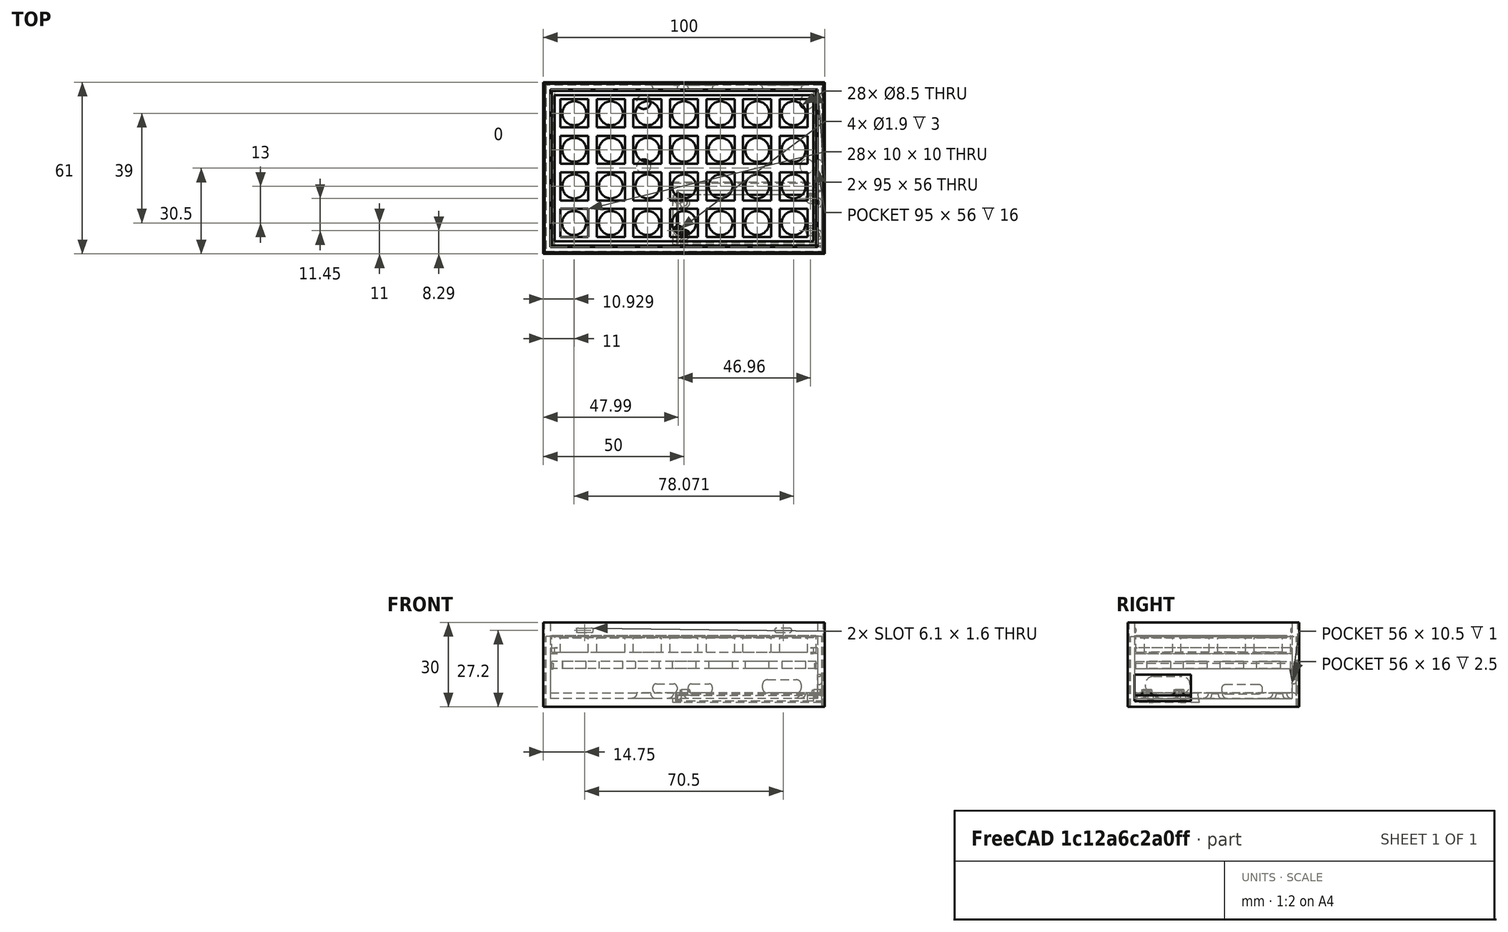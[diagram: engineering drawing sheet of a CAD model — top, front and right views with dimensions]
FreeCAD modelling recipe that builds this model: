
FCSTD DOCUMENT  (FreeCAD 1.0R39285 (Git))
Label: Contrib Cal FreeCAD
License: All rights reserved
LicenseURL: https://en.wikipedia.org/wiki/All_rights_reserved
objects: Sketcher::SketchObject×37, PartDesign::Pad×20, PartDesign::Pocket×14, PartDesign::Body×8, PartDesign::Fillet×7, Mesh::Feature×2, PartDesign::Hole×1, Measure::MeasureArea×1, Measure::MeasurePython×1
note: 208 computed .brp shape members not serialized (recipe doc carries the construction recipe); baked Part::Feature solids carry a one-line shape summary decoded from their .brp

FEATURE [Sketcher::SketchObject] Sketch
  ArcFitTolerance = 1e-06
  AttachmentSupport = -> [XY_Plane]
  FullyConstrained = true
  MakeInternals = false
  MapMode = 5
  sketch-geometry (117):
    g0: LineSegment StartX=47 StartY=-27.5 StartZ=0 EndX=47 EndY=27.5 EndZ=0
    g1: LineSegment StartX=47 StartY=27.5 StartZ=0 EndX=-47 EndY=27.5 EndZ=0
    g2: LineSegment StartX=-47 StartY=27.5 StartZ=0 EndX=-47 EndY=-27.5 EndZ=0
    g3: LineSegment StartX=-47 StartY=-27.5 StartZ=0 EndX=47 EndY=-27.5 EndZ=0
    g4: GeomPoint [constr] X=0 Y=0 Z=0
    g5: LineSegment StartX=-44 StartY=24.5 StartZ=0 EndX=-44 EndY=14.5 EndZ=0
    g6: LineSegment StartX=-44 StartY=14.5 StartZ=0 EndX=-34 EndY=14.5 EndZ=0
    g7: LineSegment StartX=-34 StartY=14.5 StartZ=0 EndX=-34 EndY=24.5 EndZ=0
    g8: LineSegment StartX=-34 StartY=24.5 StartZ=0 EndX=-44 EndY=24.5 EndZ=0
    g9: LineSegment StartX=-31 StartY=24.5 StartZ=0 EndX=-31 EndY=14.5 EndZ=0
    g10: LineSegment StartX=-31 StartY=14.5 StartZ=0 EndX=-21 EndY=14.5 EndZ=0
    g11: LineSegment StartX=-21 StartY=14.5 StartZ=0 EndX=-21 EndY=24.5 EndZ=0
    g12: LineSegment StartX=-21 StartY=24.5 StartZ=0 EndX=-31 EndY=24.5 EndZ=0
    g13: LineSegment StartX=-18 StartY=24.5 StartZ=0 EndX=-18 EndY=14.5 EndZ=0
    g14: LineSegment StartX=-18 StartY=14.5 StartZ=0 EndX=-8 EndY=14.5 EndZ=0
    g15: LineSegment StartX=-8 StartY=14.5 StartZ=0 EndX=-8 EndY=24.5 EndZ=0
    g16: LineSegment StartX=-8 StartY=24.5 StartZ=0 EndX=-18 EndY=24.5 EndZ=0
    g17: LineSegment StartX=-5 StartY=24.5 StartZ=0 EndX=-5 EndY=14.5 EndZ=0
    g18: LineSegment StartX=-5 StartY=14.5 StartZ=0 EndX=5 EndY=14.5 EndZ=0
    g19: LineSegment StartX=5 StartY=14.5 StartZ=0 EndX=5 EndY=24.5 EndZ=0
    g20: LineSegment StartX=5 StartY=24.5 StartZ=0 EndX=-5 EndY=24.5 EndZ=0
    g21: LineSegment StartX=8 StartY=24.5 StartZ=0 EndX=8 EndY=14.5 EndZ=0
    g22: LineSegment StartX=8 StartY=14.5 StartZ=0 EndX=18 EndY=14.5 EndZ=0
    g23: LineSegment StartX=18 StartY=14.5 StartZ=0 EndX=18 EndY=24.5 EndZ=0
    g24: LineSegment StartX=18 StartY=24.5 StartZ=0 EndX=8 EndY=24.5 EndZ=0
    g25: LineSegment StartX=21 StartY=24.5 StartZ=0 EndX=21 EndY=14.5 EndZ=0
    g26: LineSegment StartX=21 StartY=14.5 StartZ=0 EndX=31 EndY=14.5 EndZ=0
    g27: LineSegment StartX=31 StartY=14.5 StartZ=0 EndX=31 EndY=24.5 EndZ=0
    g28: LineSegment StartX=31 StartY=24.5 StartZ=0 EndX=21 EndY=24.5 EndZ=0
    g29: LineSegment StartX=34 StartY=24.5 StartZ=0 EndX=34 EndY=14.5 EndZ=0
    g30: LineSegment StartX=34 StartY=14.5 StartZ=0 EndX=44 EndY=14.5 EndZ=0
    g31: LineSegment StartX=44 StartY=14.5 StartZ=0 EndX=44 EndY=24.5 EndZ=0
    g32: LineSegment StartX=44 StartY=24.5 StartZ=0 EndX=34 EndY=24.5 EndZ=0
    g33: LineSegment StartX=-44 StartY=11.5 StartZ=0 EndX=-44 EndY=1.5 EndZ=0
    g34: LineSegment StartX=-44 StartY=1.5 StartZ=0 EndX=-34 EndY=1.5 EndZ=0
    g35: LineSegment StartX=-34 StartY=1.5 StartZ=0 EndX=-34 EndY=11.5 EndZ=0
    g36: LineSegment StartX=-34 StartY=11.5 StartZ=0 EndX=-44 EndY=11.5 EndZ=0
    g37: LineSegment StartX=-31 StartY=11.5 StartZ=0 EndX=-31 EndY=1.5 EndZ=0
    g38: LineSegment StartX=-31 StartY=1.5 StartZ=0 EndX=-21 EndY=1.5 EndZ=0
    g39: LineSegment StartX=-21 StartY=1.5 StartZ=0 EndX=-21 EndY=11.5 EndZ=0
    g40: LineSegment StartX=-21 StartY=11.5 StartZ=0 EndX=-31 EndY=11.5 EndZ=0
    g41: LineSegment StartX=-18 StartY=11.5 StartZ=0 EndX=-18 EndY=1.5 EndZ=0
    g42: LineSegment StartX=-18 StartY=1.5 StartZ=0 EndX=-8 EndY=1.5 EndZ=0
    g43: LineSegment StartX=-8 StartY=1.5 StartZ=0 EndX=-8 EndY=11.5 EndZ=0
    g44: LineSegment StartX=-8 StartY=11.5 StartZ=0 EndX=-18 EndY=11.5 EndZ=0
    g45: LineSegment StartX=-5 StartY=11.5 StartZ=0 EndX=-5 EndY=1.5 EndZ=0
    g46: LineSegment StartX=-5 StartY=1.5 StartZ=0 EndX=5 EndY=1.5 EndZ=0
    g47: LineSegment StartX=5 StartY=1.5 StartZ=0 EndX=5 EndY=11.5 EndZ=0
    g48: LineSegment StartX=5 StartY=11.5 StartZ=0 EndX=-5 EndY=11.5 EndZ=0
    g49: LineSegment StartX=8 StartY=11.5 StartZ=0 EndX=8 EndY=1.5 EndZ=0
    g50: LineSegment StartX=8 StartY=1.5 StartZ=0 EndX=18 EndY=1.5 EndZ=0
    g51: LineSegment StartX=18 StartY=1.5 StartZ=0 EndX=18 EndY=11.5 EndZ=0
    g52: LineSegment StartX=18 StartY=11.5 StartZ=0 EndX=8 EndY=11.5 EndZ=0
    g53: LineSegment StartX=21 StartY=11.5 StartZ=0 EndX=21 EndY=1.5 EndZ=0
    g54: LineSegment StartX=21 StartY=1.5 StartZ=0 EndX=31 EndY=1.5 EndZ=0
    g55: LineSegment StartX=31 StartY=1.5 StartZ=0 EndX=31 EndY=11.5 EndZ=0
    g56: LineSegment StartX=31 StartY=11.5 StartZ=0 EndX=21 EndY=11.5 EndZ=0
    g57: LineSegment StartX=34 StartY=11.5 StartZ=0 EndX=34 EndY=1.5 EndZ=0
    g58: LineSegment StartX=34 StartY=1.5 StartZ=0 EndX=44 EndY=1.5 EndZ=0
    g59: LineSegment StartX=44 StartY=1.5 StartZ=0 EndX=44 EndY=11.5 EndZ=0
    g60: LineSegment StartX=44 StartY=11.5 StartZ=0 EndX=34 EndY=11.5 EndZ=0
    g61: LineSegment StartX=-44 StartY=-1.5 StartZ=0 EndX=-44 EndY=-11.5 EndZ=0
    g62: LineSegment StartX=-44 StartY=-11.5 StartZ=0 EndX=-34 EndY=-11.5 EndZ=0
    g63: LineSegment StartX=-34 StartY=-11.5 StartZ=0 EndX=-34 EndY=-1.5 EndZ=0
    g64: LineSegment StartX=-34 StartY=-1.5 StartZ=0 EndX=-44 EndY=-1.5 EndZ=0
    g65: LineSegment StartX=-31 StartY=-1.5 StartZ=0 EndX=-31 EndY=-11.5 EndZ=0
    g66: LineSegment StartX=-31 StartY=-11.5 StartZ=0 EndX=-21 EndY=-11.5 EndZ=0
    g67: LineSegment StartX=-21 StartY=-11.5 StartZ=0 EndX=-21 EndY=-1.5 EndZ=0
    g68: LineSegment StartX=-21 StartY=-1.5 StartZ=0 EndX=-31 EndY=-1.5 EndZ=0
    g69: LineSegment StartX=-18 StartY=-1.5 StartZ=0 EndX=-18 EndY=-11.5 EndZ=0
    g70: LineSegment StartX=-18 StartY=-11.5 StartZ=0 EndX=-8 EndY=-11.5 EndZ=0
    g71: LineSegment StartX=-8 StartY=-11.5 StartZ=0 EndX=-8 EndY=-1.5 EndZ=0
    g72: LineSegment StartX=-8 StartY=-1.5 StartZ=0 EndX=-18 EndY=-1.5 EndZ=0
    g73: LineSegment StartX=-5 StartY=-1.5 StartZ=0 EndX=-5 EndY=-11.5 EndZ=0
    g74: LineSegment StartX=-5 StartY=-11.5 StartZ=0 EndX=5 EndY=-11.5 EndZ=0
    g75: LineSegment StartX=5 StartY=-11.5 StartZ=0 EndX=5 EndY=-1.5 EndZ=0
    g76: LineSegment StartX=5 StartY=-1.5 StartZ=0 EndX=-5 EndY=-1.5 EndZ=0
    g77: LineSegment StartX=8 StartY=-1.5 StartZ=0 EndX=8 EndY=-11.5 EndZ=0
    g78: LineSegment StartX=8 StartY=-11.5 StartZ=0 EndX=18 EndY=-11.5 EndZ=0
    g79: LineSegment StartX=18 StartY=-11.5 StartZ=0 EndX=18 EndY=-1.5 EndZ=0
    g80: LineSegment StartX=18 StartY=-1.5 StartZ=0 EndX=8 EndY=-1.5 EndZ=0
    g81: LineSegment StartX=21 StartY=-1.5 StartZ=0 EndX=21 EndY=-11.5 EndZ=0
    g82: LineSegment StartX=21 StartY=-11.5 StartZ=0 EndX=31 EndY=-11.5 EndZ=0
    g83: LineSegment StartX=31 StartY=-11.5 StartZ=0 EndX=31 EndY=-1.5 EndZ=0
    g84: LineSegment StartX=31 StartY=-1.5 StartZ=0 EndX=21 EndY=-1.5 EndZ=0
    g85: LineSegment StartX=34 StartY=-1.5 StartZ=0 EndX=34 EndY=-11.5 EndZ=0
    g86: LineSegment StartX=34 StartY=-11.5 StartZ=0 EndX=44 EndY=-11.5 EndZ=0
    g87: LineSegment StartX=44 StartY=-11.5 StartZ=0 EndX=44 EndY=-1.5 EndZ=0
    g88: LineSegment StartX=44 StartY=-1.5 StartZ=0 EndX=34 EndY=-1.5 EndZ=0
    g89: LineSegment StartX=-44 StartY=-14.5 StartZ=0 EndX=-44 EndY=-24.5 EndZ=0
    g90: LineSegment StartX=-44 StartY=-24.5 StartZ=0 EndX=-34 EndY=-24.5 EndZ=0
    g91: LineSegment StartX=-34 StartY=-24.5 StartZ=0 EndX=-34 EndY=-14.5 EndZ=0
    g92: LineSegment StartX=-34 StartY=-14.5 StartZ=0 EndX=-44 EndY=-14.5 EndZ=0
    g93: LineSegment StartX=-31 StartY=-14.5 StartZ=0 EndX=-31 EndY=-24.5 EndZ=0
    g94: LineSegment StartX=-31 StartY=-24.5 StartZ=0 EndX=-21 EndY=-24.5 EndZ=0
    g95: LineSegment StartX=-21 StartY=-24.5 StartZ=0 EndX=-21 EndY=-14.5 EndZ=0
    g96: LineSegment StartX=-21 StartY=-14.5 StartZ=0 EndX=-31 EndY=-14.5 EndZ=0
    g97: LineSegment StartX=-18 StartY=-14.5 StartZ=0 EndX=-18 EndY=-24.5 EndZ=0
    g98: LineSegment StartX=-18 StartY=-24.5 StartZ=0 EndX=-8 EndY=-24.5 EndZ=0
    g99: LineSegment StartX=-8 StartY=-24.5 StartZ=0 EndX=-8 EndY=-14.5 EndZ=0
    g100: LineSegment StartX=-8 StartY=-14.5 StartZ=0 EndX=-18 EndY=-14.5 EndZ=0
    g101: LineSegment StartX=-5 StartY=-14.5 StartZ=0 EndX=-5 EndY=-24.5 EndZ=0
    g102: LineSegment StartX=-5 StartY=-24.5 StartZ=0 EndX=5 EndY=-24.5 EndZ=0
    g103: LineSegment StartX=5 StartY=-24.5 StartZ=0 EndX=5 EndY=-14.5 EndZ=0
    g104: LineSegment StartX=5 StartY=-14.5 StartZ=0 EndX=-5 EndY=-14.5 EndZ=0
    g105: LineSegment StartX=8 StartY=-14.5 StartZ=0 EndX=8 EndY=-24.5 EndZ=0
    g106: LineSegment StartX=8 StartY=-24.5 StartZ=0 EndX=18 EndY=-24.5 EndZ=0
    g107: LineSegment StartX=18 StartY=-24.5 StartZ=0 EndX=18 EndY=-14.5 EndZ=0
    g108: LineSegment StartX=18 StartY=-14.5 StartZ=0 EndX=8 EndY=-14.5 EndZ=0
    g109: LineSegment StartX=21 StartY=-14.5 StartZ=0 EndX=21 EndY=-24.5 EndZ=0
    g110: LineSegment StartX=21 StartY=-24.5 StartZ=0 EndX=31 EndY=-24.5 EndZ=0
    g111: LineSegment StartX=31 StartY=-24.5 StartZ=0 EndX=31 EndY=-14.5 EndZ=0
    g112: LineSegment StartX=31 StartY=-14.5 StartZ=0 EndX=21 EndY=-14.5 EndZ=0
    g113: LineSegment StartX=34 StartY=-14.5 StartZ=0 EndX=34 EndY=-24.5 EndZ=0
    g114: LineSegment StartX=34 StartY=-24.5 StartZ=0 EndX=44 EndY=-24.5 EndZ=0
    g115: LineSegment StartX=44 StartY=-24.5 StartZ=0 EndX=44 EndY=-14.5 EndZ=0
    g116: LineSegment StartX=44 StartY=-14.5 StartZ=0 EndX=34 EndY=-14.5 EndZ=0
  constraints (348):
    c: Coincident(g0,g1)
    c: Coincident(g1,g2)
    c: Coincident(g2,g3)
    c: Coincident(g3,g0)
    c: Vertical(g0)
    c: Vertical(g2)
    c: Horizontal(g1)
    c: Horizontal(g3)
    c: Symmetric(g2,g0,g4)
    c: Coincident(g4,g-1)
    c: DistanceX(g1,g1) = 94
    c: DistanceY(g2,g2) = 55
    c: Coincident(g5,g6)
    c: Coincident(g6,g7)
    c: Coincident(g7,g8)
    c: Coincident(g8,g5)
    c: Vertical(g5)
    c: Vertical(g7)
    c: Horizontal(g6)
    c: Horizontal(g8)
    c: DistanceX(g8,g8) = 10
    c: DistanceY(g7,g7) = 10
    c: Coincident(g9,g10)
    c: Coincident(g10,g11)
    c: Coincident(g11,g12)
    c: Coincident(g12,g9)
    c: Vertical(g9)
    c: Vertical(g11)
    c: Horizontal(g10)
    c: Horizontal(g12)
    c: Coincident(g13,g14)
    c: Coincident(g14,g15)
    c: Coincident(g15,g16)
    c: Coincident(g16,g13)
    c: Vertical(g13)
    c: Vertical(g15)
    c: Horizontal(g14)
    c: Horizontal(g16)
    c: Coincident(g17,g18)
    c: Coincident(g18,g19)
    c: Coincident(g19,g20)
    c: Coincident(g20,g17)
    c: Vertical(g17)
    c: Vertical(g19)
    c: Horizontal(g18)
    c: Horizontal(g20)
    c: Coincident(g21,g22)
    c: Coincident(g22,g23)
    c: Coincident(g23,g24)
    c: Coincident(g24,g21)
    c: Vertical(g21)
    c: Vertical(g23)
    c: Horizontal(g22)
    c: Horizontal(g24)
    c: Coincident(g25,g26)
    c: Coincident(g26,g27)
    c: Coincident(g27,g28)
    c: Coincident(g28,g25)
    c: Vertical(g25)
    c: Vertical(g27)
    c: Horizontal(g26)
    c: Horizontal(g28)
    c: DistanceX(g12,g12) = 10
    c: DistanceY(g11,g11) = 10
    c: DistanceX(g16,g16) = 10
    c: DistanceY(g15,g15) = 10
    c: DistanceX(g20,g20) = 10
    c: DistanceX(g24,g24) = 10
    c: DistanceX(g28,g28) = 10
    c: DistanceX(g1,g5) = 3
    c: DistanceY(g5,g1) = 3
    c: DistanceX(g7,g9) = 3
    c: DistanceY(g9,g7) = 0
    c: DistanceX(g11,g13) = 3
    c: DistanceY(g13,g11) = 0
    c: DistanceX(g15,g17) = 3
    c: DistanceY(g17,g15) = 0
    c: DistanceX(g19,g21) = 3
    c: DistanceY(g21,g19) = 0
    c: DistanceX(g23,g25) = 3
    c: DistanceY(g25,g23) = 0
    c: DistanceY(g21,g21) = 10
    c: DistanceY(g17,g17) = 10
    c: DistanceY(g25,g25) = 10
    c: Coincident(g29,g30)
    c: Coincident(g30,g31)
    c: Coincident(g31,g32)
    c: Coincident(g32,g29)
    c: Vertical(g29)
    c: Vertical(g31)
    c: Horizontal(g30)
    c: Horizontal(g32)
    c: DistanceX(g32,g32) = 10
    c: DistanceY(g29,g29) = 10
    c: DistanceX(g27,g29) = 3
    c: DistanceY(g29,g27) = 0
    c: Coincident(g33,g34)
    c: Coincident(g34,g35)
    c: Coincident(g35,g36)
    c: Coincident(g36,g33)
    c: Vertical(g33)
    c: Vertical(g35)
    c: Horizontal(g34)
    c: Horizontal(g36)
    c: Coincident(g37,g38)
    c: Coincident(g38,g39)
    c: Coincident(g39,g40)
    c: Coincident(g40,g37)
    c: Vertical(g37)
    c: Vertical(g39)
    c: Horizontal(g38)
    c: Horizontal(g40)
    c: Coincident(g41,g42)
    c: Coincident(g42,g43)
    c: Coincident(g43,g44)
    c: Coincident(g44,g41)
    c: Vertical(g41)
    c: Vertical(g43)
    c: Horizontal(g42)
    c: Horizontal(g44)
    c: Coincident(g45,g46)
    c: Coincident(g46,g47)
    c: Coincident(g47,g48)
    c: Coincident(g48,g45)
    c: Vertical(g45)
    c: Vertical(g47)
    c: Horizontal(g46)
    c: Horizontal(g48)
    c: Coincident(g49,g50)
    c: Coincident(g50,g51)
    c: Coincident(g51,g52)
    c: Coincident(g52,g49)
    c: Vertical(g49)
    c: Vertical(g51)
    c: Horizontal(g50)
    c: Horizontal(g52)
    c: Coincident(g53,g54)
    c: Coincident(g54,g55)
    c: Coincident(g55,g56)
    c: Coincident(g56,g53)
    c: Vertical(g53)
    c: Vertical(g55)
    c: Horizontal(g54)
    c: Horizontal(g56)
    c: Coincident(g57,g58)
    c: Coincident(g58,g59)
    c: Coincident(g59,g60)
    c: Coincident(g60,g57)
    c: Vertical(g57)
    c: Vertical(g59)
    c: Horizontal(g58)
    c: Horizontal(g60)
    c: DistanceX(g36,g36) = 10
    c: DistanceX(g40,g40) = 10
    c: DistanceX(g44,g44) = 10
    c: DistanceX(g48,g48) = 10
    c: DistanceX(g52,g52) = 10
    c: DistanceX(g56,g56) = 10
    c: DistanceX(g60,g60) = 10
    c: DistanceY(g33,g33) = 10
    c: DistanceY(g37,g37) = 10
    c: DistanceY(g41,g41) = 10
    c: DistanceY(g45,g45) = 10
    c: DistanceY(g49,g49) = 10
    c: DistanceY(g53,g53) = 10
    c: DistanceY(g57,g57) = 10
    c: DistanceY(g37,g35) = 0
    c: DistanceY(g41,g39) = 0
    c: DistanceY(g45,g43) = 0
    c: DistanceY(g49,g47) = 0
    c: DistanceY(g53,g51) = 0
    c: DistanceY(g57,g55) = 0
    c: DistanceX(g35,g37) = 3
    c: DistanceX(g39,g41) = 3
    c: DistanceX(g43,g45) = 3
    c: DistanceX(g47,g49) = 3
    c: DistanceX(g51,g53) = 3
    c: DistanceX(g55,g57) = 3
    c: DistanceX(g5,g33) = 0
    c: Coincident(g61,g62)
    c: Coincident(g62,g63)
    c: Coincident(g63,g64)
    c: Coincident(g64,g61)
    c: Vertical(g61)
    c: Vertical(g63)
    c: Horizontal(g62)
    c: Horizontal(g64)
    c: Coincident(g65,g66)
    c: Coincident(g66,g67)
    c: Coincident(g67,g68)
    c: Coincident(g68,g65)
    c: Vertical(g65)
    c: Vertical(g67)
    c: Horizontal(g66)
    c: Horizontal(g68)
    c: Coincident(g69,g70)
    c: Coincident(g70,g71)
    c: Coincident(g71,g72)
    c: Coincident(g72,g69)
    c: Vertical(g69)
    c: Vertical(g71)
    c: Horizontal(g70)
    c: Horizontal(g72)
    c: Coincident(g73,g74)
    c: Coincident(g74,g75)
    c: Coincident(g75,g76)
    c: Coincident(g76,g73)
    c: Vertical(g73)
    c: Vertical(g75)
    c: Horizontal(g74)
    c: Horizontal(g76)
    c: Coincident(g77,g78)
    c: Coincident(g78,g79)
    c: Coincident(g79,g80)
    c: Coincident(g80,g77)
    c: Vertical(g77)
    c: Vertical(g79)
    c: Horizontal(g78)
    c: Horizontal(g80)
    c: Coincident(g81,g82)
    c: Coincident(g82,g83)
    c: Coincident(g83,g84)
    c: Coincident(g84,g81)
    c: Vertical(g81)
    c: Vertical(g83)
    c: Horizontal(g82)
    c: Horizontal(g84)
    c: Coincident(g85,g86)
    c: Coincident(g86,g87)
    c: Coincident(g87,g88)
    c: Coincident(g88,g85)
    c: Vertical(g85)
    c: Vertical(g87)
    c: Horizontal(g86)
    c: Horizontal(g88)
    c: DistanceX(g64,g64) = 10
    c: DistanceX(g68,g68) = 10
    c: DistanceX(g72,g72) = 10
    c: DistanceX(g76,g76) = 10
    c: DistanceX(g80,g80) = 10
    c: DistanceX(g84,g84) = 10
    c: DistanceX(g88,g88) = 10
    c: DistanceY(g61,g61) = 10
    c: DistanceY(g65,g65) = 10
    c: DistanceY(g69,g69) = 10
    c: DistanceY(g73,g73) = 10
    c: DistanceY(g77,g77) = 10
    c: DistanceY(g81,g81) = 10
    c: DistanceY(g85,g85) = 10
    c: DistanceX(g63,g65) = 3
    c: DistanceX(g67,g69) = 3
    c: DistanceX(g71,g73) = 3
    c: DistanceX(g75,g77) = 3
    c: DistanceX(g79,g81) = 3
    c: DistanceX(g83,g85) = 3
    c: DistanceY(g65,g63) = 0
    c: DistanceY(g69,g67) = 0
    c: DistanceY(g73,g71) = 0
    c: DistanceY(g77,g75) = 0
    c: DistanceY(g79,g81) = 0
    c: DistanceY(g83,g85) = 0
    c: DistanceX(g61,g33) = 0
    c: DistanceY(g61,g33) = 3
    c: DistanceY(g33,g5) = 3
    c: Coincident(g89,g90)
    c: Coincident(g90,g91)
    c: Coincident(g91,g92)
    c: Coincident(g92,g89)
    c: Vertical(g89)
    c: Vertical(g91)
    c: Horizontal(g90)
    c: Horizontal(g92)
    c: Coincident(g93,g94)
    c: Coincident(g94,g95)
    c: Coincident(g95,g96)
    c: Coincident(g96,g93)
    c: Vertical(g93)
    c: Vertical(g95)
    c: Horizontal(g94)
    c: Horizontal(g96)
    c: Coincident(g97,g98)
    c: Coincident(g98,g99)
    c: Coincident(g99,g100)
    c: Coincident(g100,g97)
    c: Vertical(g97)
    c: Vertical(g99)
    c: Horizontal(g98)
    c: Horizontal(g100)
    c: Coincident(g101,g102)
    c: Coincident(g102,g103)
    c: Coincident(g103,g104)
    c: Coincident(g104,g101)
    c: Vertical(g101)
    c: Vertical(g103)
    c: Horizontal(g102)
    c: Horizontal(g104)
    c: Coincident(g105,g106)
    c: Coincident(g106,g107)
    c: Coincident(g107,g108)
    c: Coincident(g108,g105)
    c: Vertical(g105)
    c: Vertical(g107)
    c: Horizontal(g106)
    c: Horizontal(g108)
    c: Coincident(g109,g110)
    c: Coincident(g110,g111)
    c: Coincident(g111,g112)
    c: Coincident(g112,g109)
    c: Vertical(g109)
    c: Vertical(g111)
    c: Horizontal(g110)
    c: Horizontal(g112)
    c: Coincident(g113,g114)
    c: Coincident(g114,g115)
    c: Coincident(g115,g116)
    c: Coincident(g116,g113)
    c: Vertical(g113)
    c: Vertical(g115)
    c: Horizontal(g114)
    c: Horizontal(g116)
    c: DistanceX(g92,g92) = 10
    c: DistanceX(g96,g96) = 10
    c: DistanceX(g100,g100) = 10
    c: DistanceX(g104,g104) = 10
    c: DistanceX(g108,g108) = 10
    c: DistanceX(g112,g112) = 10
    c: DistanceX(g116,g116) = 10
    c: DistanceY(g89,g89) = 10
    c: DistanceY(g93,g93) = 10
    c: DistanceY(g97,g97) = 10
    c: DistanceY(g101,g101) = 10
    c: DistanceY(g105,g105) = 10
    c: DistanceY(g109,g109) = 10
    c: DistanceY(g113,g113) = 10
    c: DistanceX(g91,g93) = 3
    c: DistanceX(g95,g97) = 3
    c: DistanceX(g99,g101) = 3
    c: DistanceX(g103,g105) = 3
    c: DistanceX(g107,g109) = 3
    c: DistanceX(g111,g113) = 3
    c: DistanceY(g111,g113) = 0
    c: DistanceY(g109,g107) = 0
    c: DistanceY(g105,g103) = 0
    c: DistanceY(g101,g99) = 0
    c: DistanceY(g97,g95) = 0
    c: DistanceY(g93,g91) = 0
    c: DistanceX(g61,g89) = 0
    c: DistanceY(g89,g61) = 3
FEATURE [PartDesign::Pad] Pad
  Direction = (0,0,1)
  Length = 6
  Length2 = 10
  Profile = -> Sketch
  ReferenceAxis = -> Sketch [N_Axis]
  Refine = true
  Suppressed = false
  Type = 0
FEATURE [Sketcher::SketchObject] Sketch002
  ArcFitTolerance = 1e-06
  AttachmentSupport = -> [XY_Plane001]
  FullyConstrained = true
  MakeInternals = false
  MapMode = 5
  sketch-geometry (33):
    g0: LineSegment StartX=47 StartY=-27.5 StartZ=0 EndX=47 EndY=27.5 EndZ=0
    g1: LineSegment StartX=47 StartY=27.5 StartZ=0 EndX=-47 EndY=27.5 EndZ=0
    g2: LineSegment StartX=-47 StartY=27.5 StartZ=0 EndX=-47 EndY=-27.5 EndZ=0
    g3: LineSegment StartX=-47 StartY=-27.5 StartZ=0 EndX=47 EndY=-27.5 EndZ=0
    g4: GeomPoint [constr] X=0 Y=0 Z=0
    g5: Circle CenterX=-39 CenterY=19.5 CenterZ=0 NormalX=0 NormalY=0 NormalZ=1 AngleXU=0 Radius=4.25
    g6: Circle CenterX=-26 CenterY=19.5 CenterZ=0 NormalX=0 NormalY=0 NormalZ=1 AngleXU=0 Radius=4.25
    g7: Circle CenterX=-13 CenterY=19.5 CenterZ=0 NormalX=0 NormalY=0 NormalZ=1 AngleXU=0 Radius=4.25
    g8: Circle CenterX=-4e-16 CenterY=19.5 CenterZ=0 NormalX=0 NormalY=0 NormalZ=1 AngleXU=0 Radius=4.25
    g9: Circle CenterX=13 CenterY=19.5 CenterZ=0 NormalX=0 NormalY=0 NormalZ=1 AngleXU=0 Radius=4.25
    g10: Circle CenterX=26 CenterY=19.5 CenterZ=0 NormalX=0 NormalY=0 NormalZ=1 AngleXU=0 Radius=4.25
    g11: Circle CenterX=39 CenterY=19.5 CenterZ=0 NormalX=0 NormalY=0 NormalZ=1 AngleXU=0 Radius=4.25
    g12: Circle CenterX=-39 CenterY=6.5 CenterZ=0 NormalX=0 NormalY=0 NormalZ=1 AngleXU=0 Radius=4.25
    g13: Circle CenterX=-26 CenterY=6.5 CenterZ=0 NormalX=0 NormalY=0 NormalZ=1 AngleXU=0 Radius=4.25
    g14: Circle CenterX=-13 CenterY=6.5 CenterZ=0 NormalX=0 NormalY=0 NormalZ=1 AngleXU=0 Radius=4.25
    g15: Circle CenterX=0 CenterY=6.5 CenterZ=0 NormalX=0 NormalY=0 NormalZ=1 AngleXU=0 Radius=4.25
    g16: Circle CenterX=13 CenterY=6.5 CenterZ=0 NormalX=0 NormalY=0 NormalZ=1 AngleXU=0 Radius=4.25
    g17: Circle CenterX=26 CenterY=6.5 CenterZ=0 NormalX=0 NormalY=0 NormalZ=1 AngleXU=0 Radius=4.25
    g18: Circle CenterX=39 CenterY=6.5 CenterZ=0 NormalX=0 NormalY=0 NormalZ=1 AngleXU=0 Radius=4.25
    g19: Circle CenterX=-39 CenterY=-6.5 CenterZ=0 NormalX=0 NormalY=0 NormalZ=1 AngleXU=0 Radius=4.25
    g20: Circle CenterX=-26 CenterY=-6.5 CenterZ=0 NormalX=0 NormalY=0 NormalZ=1 AngleXU=0 Radius=4.25
    g21: Circle CenterX=-13 CenterY=-6.5 CenterZ=0 NormalX=0 NormalY=0 NormalZ=1 AngleXU=0 Radius=4.25
    g22: Circle CenterX=0 CenterY=-6.5 CenterZ=0 NormalX=0 NormalY=0 NormalZ=1 AngleXU=0 Radius=4.25
    g23: Circle CenterX=13 CenterY=-6.5 CenterZ=0 NormalX=0 NormalY=0 NormalZ=1 AngleXU=0 Radius=4.25
    g24: Circle CenterX=26 CenterY=-6.5 CenterZ=0 NormalX=0 NormalY=0 NormalZ=1 AngleXU=0 Radius=4.25
    g25: Circle CenterX=39 CenterY=-6.5 CenterZ=0 NormalX=0 NormalY=0 NormalZ=1 AngleXU=0 Radius=4.25
    g26: Circle CenterX=-39.0713 CenterY=-19.5 CenterZ=0 NormalX=0 NormalY=0 NormalZ=1 AngleXU=0 Radius=4.25
    g27: Circle CenterX=-26 CenterY=-19.5 CenterZ=0 NormalX=0 NormalY=0 NormalZ=1 AngleXU=0 Radius=4.25
    g28: Circle CenterX=-13 CenterY=-19.5 CenterZ=0 NormalX=0 NormalY=0 NormalZ=1 AngleXU=0 Radius=4.25
    g29: Circle CenterX=0 CenterY=-19.5 CenterZ=0 NormalX=0 NormalY=0 NormalZ=1 AngleXU=0 Radius=4.25
    g30: Circle CenterX=13 CenterY=-19.5 CenterZ=0 NormalX=0 NormalY=0 NormalZ=1 AngleXU=0 Radius=4.25
    g31: Circle CenterX=26 CenterY=-19.5 CenterZ=0 NormalX=0 NormalY=0 NormalZ=1 AngleXU=0 Radius=4.25
    g32: Circle CenterX=39 CenterY=-19.5 CenterZ=0 NormalX=0 NormalY=0 NormalZ=1 AngleXU=0 Radius=4.25
  constraints (96):
    c: Coincident(g0,g1)
    c: Coincident(g1,g2)
    c: Coincident(g2,g3)
    c: Coincident(g3,g0)
    c: Vertical(g0)
    c: Vertical(g2)
    c: Horizontal(g1)
    c: Horizontal(g3)
    c: Symmetric(g2,g0,g4)
    c: Coincident(g4,g-1)
    c: DistanceX(g1,g1) = 94
    c: DistanceY(g2,g2) = 55
    c: Equal(g5,g6)
    c: Equal(g6,g7)
    c: Equal(g7,g8)
    c: Equal(g8,g9)
    c: Equal(g9,g10)
    c: Equal(g10,g11)
    c: Diameter(g5) = 8.5
    c: DistanceY(g5,g1) = 8
    c: DistanceY(g5,g6) = 0
    c: DistanceY(g6,g7) = 0
    c: DistanceY(g7,g8) = 0
    c: DistanceY(g8,g9) = 0
    c: DistanceY(g9,g10) = 0
    c: DistanceY(g10,g11) = 0
    c: DistanceX(g5,g6) = 13
    c: DistanceX(g6,g7) = 13
    c: DistanceX(g7,g8) = 13
    c: DistanceX(g8,g9) = 13
    c: DistanceX(g9,g10) = 13
    c: DistanceX(g10,g11) = 13
    c: DistanceX(g1,g5) = 8
    c: PointOnObject(g15,g-2)
    c: DistanceX(g12,g13) = 13
    c: DistanceX(g13,g14) = 13
    c: DistanceX(g14,g15) = 13
    c: DistanceX(g15,g16) = 13
    c: DistanceX(g16,g17) = 13
    c: DistanceX(g17,g18) = 13
    c: Equal(g12,g13)
    c: Equal(g13,g14)
    c: Equal(g14,g15)
    c: Equal(g15,g16)
    c: Equal(g16,g17)
    c: Equal(g17,g18)
    c: Equal(g5,g12)
    c: DistanceY(g12,g5) = 13
    c: Horizontal(g12,g13)
    c: Horizontal(g13,g14)
    c: Horizontal(g15,g16)
    c: Horizontal(g17,g18)
    c: Horizontal(g17,g16)
    c: Horizontal(g15,g14)
    c: PointOnObject(g22,g-2)
    c: Horizontal(g19,g20)
    c: Horizontal(g20,g21)
    c: Horizontal(g21,g22)
    c: Horizontal(g22,g23)
    c: Horizontal(g23,g24)
    c: Horizontal(g24,g25)
    c: Equal(g19,g20)
    c: Equal(g20,g21)
    c: Equal(g21,g22)
    c: Equal(g22,g23)
    c: Equal(g23,g25)
    c: Equal(g24,g23)
    c: Equal(g19,g12)
    c: DistanceX(g19,g20) = 13
    c: DistanceX(g20,g21) = 13
    c: DistanceX(g21,g22) = 13
    c: DistanceX(g22,g23) = 13
    c: DistanceX(g23,g24) = 13
    c: DistanceX(g24,g25) = 13
    c: PointOnObject(g29,g-2)
    c: Equal(g26,g27)
    c: Equal(g27,g28)
    c: Equal(g28,g29)
    c: Equal(g29,g30)
    c: Equal(g30,g31)
    c: Equal(g31,g32)
    c: Equal(g32,g25)
    c: Horizontal(g26,g27)
    c: Horizontal(g27,g28)
    c: Horizontal(g28,g29)
    c: Horizontal(g29,g30)
    c: Horizontal(g30,g31)
    c: Horizontal(g31,g32)
    c: DistanceX(g26,g27) = 13.0713
    c: DistanceX(g27,g28) = 13
    c: DistanceX(g28,g29) = 13
    c: DistanceX(g29,g30) = 13
    c: DistanceX(g30,g31) = 13
    c: DistanceX(g31,g32) = 13
    c: DistanceY(g19,g12) = 13
    c: DistanceY(g26,g19) = 13
FEATURE [PartDesign::Pad] Pad001
  Direction = (0,0,1)
  Length = 2.5
  Length2 = 10
  Profile = -> Sketch002
  ReferenceAxis = -> Sketch002 [N_Axis]
  Refine = true
  Suppressed = false
  Type = 0
FEATURE [PartDesign::Body] Body001  label="LED Panel"
  AllowCompound = false
  Group = -> [Sketch002,Pad001]
  Origin = -> Origin001
  Placement = pos=(0,0,13.6) rot=(0,0,1;0rad)
  Tip = -> Pad001
FEATURE [Sketcher::SketchObject] Sketch003
  ArcFitTolerance = 1e-06
  AttachmentSupport = -> [XY_Plane002]
  FullyConstrained = true
  MakeInternals = false
  MapMode = 5
  sketch-geometry (5):
    g0: LineSegment StartX=49.5 StartY=-30 StartZ=0 EndX=49.5 EndY=30 EndZ=0
    g1: LineSegment StartX=49.5 StartY=30 StartZ=0 EndX=-49.5 EndY=30 EndZ=0
    g2: LineSegment StartX=-49.5 StartY=30 StartZ=0 EndX=-49.5 EndY=-30 EndZ=0
    g3: LineSegment StartX=-49.5 StartY=-30 StartZ=0 EndX=49.5 EndY=-30 EndZ=0
    g4: GeomPoint [constr] X=0 Y=0 Z=0
  constraints (12):
    c: Coincident(g0,g1)
    c: Coincident(g1,g2)
    c: Coincident(g2,g3)
    c: Coincident(g3,g0)
    c: Vertical(g0)
    c: Vertical(g2)
    c: Horizontal(g1)
    c: Horizontal(g3)
    c: Symmetric(g2,g0,g4)
    c: Coincident(g4,g-1)
    c: DistanceX(g1,g1) = 99
    c: DistanceY(g2,g2) = 60
FEATURE [PartDesign::Pad] Pad002
  Direction = (0,0,1)
  Length = 30
  Length2 = 10
  Profile = -> Sketch003
  ReferenceAxis = -> Sketch003 [N_Axis]
  Refine = true
  Suppressed = false
  Type = 0
FEATURE [Sketcher::SketchObject] Sketch004
  ArcFitTolerance = 1e-06
  AttachmentSupport = -> [Pad002]
  FullyConstrained = true
  MakeInternals = false
  MapMode = 5
  Placement = pos=(0,0,30) rot=(0,0,1;0rad)
  sketch-geometry (5):
    g0: LineSegment StartX=47.5 StartY=-28 StartZ=0 EndX=47.5 EndY=28 EndZ=0
    g1: LineSegment StartX=47.5 StartY=28 StartZ=0 EndX=-47.5 EndY=28 EndZ=0
    g2: LineSegment StartX=-47.5 StartY=28 StartZ=0 EndX=-47.5 EndY=-28 EndZ=0
    g3: LineSegment StartX=-47.5 StartY=-28 StartZ=0 EndX=47.5 EndY=-28 EndZ=0
    g4: GeomPoint [constr] X=0 Y=0 Z=0
  constraints (12):
    c: Coincident(g0,g1)
    c: Coincident(g1,g2)
    c: Coincident(g2,g3)
    c: Coincident(g3,g0)
    c: Vertical(g0)
    c: Vertical(g2)
    c: Horizontal(g1)
    c: Horizontal(g3)
    c: Symmetric(g2,g0,g4)
    c: Coincident(g4,g-1)
    c: DistanceX(g1,g1) = 95
    c: DistanceY(g2,g2) = 56
FEATURE [PartDesign::Pocket] Pocket001
  BaseFeature = -> Pad002
  Direction = (0,0,-1)
  Length = 27
  Length2 = 5
  Profile = -> Sketch004
  ReferenceAxis = -> Sketch004 [N_Axis]
  Refine = true
  Suppressed = false
  Type = 0
FEATURE [Sketcher::SketchObject] Sketch005
  ArcFitTolerance = 1e-06
  AttachmentSupport = -> [Pocket001]
  ExternalGeometry = -> [Pocket001]
  FullyConstrained = true
  MakeInternals = false
  MapMode = 5
  Placement = pos=(0,28,0) rot=(1,0,0;1.5708rad)
  sketch-geometry (8):
    g0: ArcOfCircle CenterX=-37.5 CenterY=27.2 CenterZ=0 NormalX=0 NormalY=0 NormalZ=1 AngleXU=0 Radius=0.8 StartAngle=1.5708 EndAngle=4.71239
    g1: ArcOfCircle CenterX=-33 CenterY=27.2 CenterZ=0 NormalX=0 NormalY=0 NormalZ=1 AngleXU=0 Radius=0.8 StartAngle=4.71239 EndAngle=7.85398
    g2: LineSegment StartX=-37.5 StartY=28 StartZ=0 EndX=-33 EndY=28 EndZ=0
    g3: LineSegment StartX=-37.5 StartY=26.4 StartZ=0 EndX=-33 EndY=26.4 EndZ=0
    g4: ArcOfCircle CenterX=33 CenterY=27.2 CenterZ=0 NormalX=0 NormalY=0 NormalZ=1 AngleXU=0 Radius=0.8 StartAngle=1.5708 EndAngle=4.71239
    g5: ArcOfCircle CenterX=37.5 CenterY=27.2 CenterZ=0 NormalX=0 NormalY=0 NormalZ=1 AngleXU=0 Radius=0.8 StartAngle=4.71239 EndAngle=7.85398
    g6: LineSegment StartX=33 StartY=28 StartZ=0 EndX=37.5 EndY=28 EndZ=0
    g7: LineSegment StartX=33 StartY=26.4 StartZ=0 EndX=37.5 EndY=26.4 EndZ=0
  constraints (20):
    c: Tangent(g0,g2) = 1.5708
    c: Tangent(g0,g3) = -1.5708
    c: Tangent(g1,g2) = 1.5708
    c: Tangent(g1,g3) = -1.5708
    c: Equal(g0,g1)
    c: Horizontal(g2)
    c: Radius(g1) = 0.8
    c: DistanceX(g2,g2) = 4.5
    c: DistanceY(g0,g-3) = 2
    c: DistanceX(g-3,g0) = 10
    c: Tangent(g4,g6) = 1.5708
    c: Tangent(g4,g7) = -1.5708
    c: Tangent(g5,g6) = 1.5708
    c: Tangent(g5,g7) = -1.5708
    c: Equal(g4,g5)
    c: Horizontal(g6)
    c: DistanceX(g6,g6) = 4.5
    c: Radius(g5) = 0.8
    c: DistanceY(g5,g-3) = 2
    c: DistanceX(g5,g-3) = 10
FEATURE [PartDesign::Pad] Pad003
  BaseFeature = -> Pocket001
  Direction = (0,-1,2e-16)
  Length = 0.5
  Length2 = 10
  Profile = -> Sketch005
  ReferenceAxis = -> Sketch005 [N_Axis]
  Refine = true
  Suppressed = false
  Type = 0
FEATURE [Sketcher::SketchObject] Sketch006
  ArcFitTolerance = 1e-06
  AttachmentSupport = -> [Pad003]
  ExternalGeometry = -> [Pad003]
  FullyConstrained = true
  MakeInternals = false
  MapMode = 5
  Placement = pos=(0,-28,0) rot=(0,0.707107,0.707107;3.14159rad)
  sketch-geometry (8):
    g0: ArcOfCircle CenterX=-37.5 CenterY=27.2 CenterZ=0 NormalX=0 NormalY=0 NormalZ=1 AngleXU=0 Radius=0.8 StartAngle=1.5708 EndAngle=4.71239
    g1: ArcOfCircle CenterX=-33 CenterY=27.2 CenterZ=0 NormalX=0 NormalY=0 NormalZ=1 AngleXU=0 Radius=0.8 StartAngle=4.71239 EndAngle=7.85398
    g2: LineSegment StartX=-37.5 StartY=28 StartZ=0 EndX=-33 EndY=28 EndZ=0
    g3: LineSegment StartX=-37.5 StartY=26.4 StartZ=0 EndX=-33 EndY=26.4 EndZ=0
    g4: ArcOfCircle CenterX=33 CenterY=27.2 CenterZ=0 NormalX=0 NormalY=0 NormalZ=1 AngleXU=0 Radius=0.8 StartAngle=1.5708 EndAngle=4.71239
    g5: ArcOfCircle CenterX=37.5 CenterY=27.2 CenterZ=0 NormalX=0 NormalY=0 NormalZ=1 AngleXU=0 Radius=0.8 StartAngle=4.71239 EndAngle=7.85398
    g6: LineSegment StartX=33 StartY=28 StartZ=0 EndX=37.5 EndY=28 EndZ=0
    g7: LineSegment StartX=33 StartY=26.4 StartZ=0 EndX=37.5 EndY=26.4 EndZ=0
  constraints (20):
    c: Tangent(g0,g2) = 1.5708
    c: Tangent(g0,g3) = -1.5708
    c: Tangent(g1,g2) = 1.5708
    c: Tangent(g1,g3) = -1.5708
    c: Equal(g0,g1)
    c: Horizontal(g2)
    c: Tangent(g4,g6) = 1.5708
    c: Tangent(g4,g7) = -1.5708
    c: Tangent(g5,g6) = 1.5708
    c: Tangent(g5,g7) = -1.5708
    c: Equal(g4,g5)
    c: Horizontal(g6)
    c: DistanceX(g2,g2) = 4.5
    c: DistanceX(g6,g6) = 4.5
    c: Radius(g1) = 0.8
    c: Radius(g4) = 0.8
    c: DistanceX(g-3,g0) = 10
    c: DistanceY(g0,g-3) = 2
    c: DistanceY(g4,g1) = 0
    c: DistanceX(g5,g-3) = 10
FEATURE [PartDesign::Pad] Pad004
  BaseFeature = -> Pad003
  Direction = (0,1,-2e-16)
  Length = 0.5
  Length2 = 10
  Profile = -> Sketch006
  ReferenceAxis = -> Sketch006 [N_Axis]
  Refine = true
  Suppressed = false
  Type = 0
FEATURE [Sketcher::SketchObject] Sketch007
  ArcFitTolerance = 1e-06
  AttachmentSupport = -> [Pad004]
  ExternalGeometry = -> [Pad004]
  FullyConstrained = true
  MakeInternals = false
  MapMode = 5
  Placement = pos=(47.5,0,0) rot=(0.57735,-0.57735,-0.57735;2.0944rad)
  sketch-geometry (4):
    g0: LineSegment StartX=-28 StartY=21 StartZ=0 EndX=-28 EndY=19 EndZ=0
    g1: LineSegment StartX=-28 StartY=19 StartZ=0 EndX=28 EndY=19 EndZ=0
    g2: LineSegment StartX=28 StartY=19 StartZ=0 EndX=28 EndY=21 EndZ=0
    g3: LineSegment StartX=28 StartY=21 StartZ=0 EndX=-28 EndY=21 EndZ=0
  constraints (12):
    c: Coincident(g0,g1)
    c: Coincident(g1,g2)
    c: Coincident(g2,g3)
    c: Coincident(g3,g0)
    c: Vertical(g0)
    c: Vertical(g2)
    c: Horizontal(g1)
    c: Horizontal(g3)
    c: PointOnObject(g0,g-4)
    c: PointOnObject(g1,g-5)
    c: DistanceY(g0,g-4) = 9
    c: DistanceY(g0,g0) = 2
FEATURE [PartDesign::Pad] Pad005
  BaseFeature = -> Pad004
  Direction = (-1,0,0)
  Length = 1.5
  Length2 = 10
  Profile = -> Sketch007
  ReferenceAxis = -> Sketch007 [N_Axis]
  Refine = true
  Suppressed = false
  Type = 0
FEATURE [Sketcher::SketchObject] Sketch008
  ArcFitTolerance = 1e-06
  AttachmentSupport = -> [Pad005]
  ExternalGeometry = -> [Pad005]
  FullyConstrained = true
  MakeInternals = false
  MapMode = 5
  Placement = pos=(-47.5,0,0) rot=(0.57735,0.57735,0.57735;2.0944rad)
  sketch-geometry (4):
    g0: LineSegment StartX=-28 StartY=21 StartZ=0 EndX=-28 EndY=19 EndZ=0
    g1: LineSegment StartX=-28 StartY=19 StartZ=0 EndX=28 EndY=19 EndZ=0
    g2: LineSegment StartX=28 StartY=19 StartZ=0 EndX=28 EndY=21 EndZ=0
    g3: LineSegment StartX=28 StartY=21 StartZ=0 EndX=-28 EndY=21 EndZ=0
  constraints (12):
    c: Coincident(g0,g1)
    c: Coincident(g1,g2)
    c: Coincident(g2,g3)
    c: Coincident(g3,g0)
    c: Vertical(g0)
    c: Vertical(g2)
    c: Horizontal(g1)
    c: Horizontal(g3)
    c: PointOnObject(g0,g-3)
    c: PointOnObject(g1,g-4)
    c: DistanceY(g0,g-3) = 9
    c: DistanceY(g0,g0) = 2
FEATURE [PartDesign::Pad] Pad006
  BaseFeature = -> Pad005
  Direction = (1,0,0)
  Length = 1.5
  Length2 = 10
  Profile = -> Sketch008
  ReferenceAxis = -> Sketch008 [N_Axis]
  Refine = true
  Suppressed = false
  Type = 0
FEATURE [PartDesign::Fillet] Fillet
  Base = -> Pad006 [Edge22,Edge47,Edge28,Edge41]
  BaseFeature = -> Pad006
  Radius = 1
  Refine = true
  SupportTransform = false
  Suppressed = false
  UseAllEdges = false
FEATURE [PartDesign::Fillet] Fillet001
  Base = -> Fillet [Face32,Face31,Face43,Face42]
  BaseFeature = -> Fillet
  Radius = 0.45
  Refine = true
  SupportTransform = false
  Suppressed = false
  UseAllEdges = false
FEATURE [PartDesign::Body] Body002  label="Case v1"
  AllowCompound = false
  Group = -> [Sketch003,Pad002,Sketch004,Pocket001,Sketch005,Pad003,Sketch006,Pad004,Sketch007,Pad005,Sketch008,Pad006,Fillet,Fillet001]
  Origin = -> Origin002
  Tip = -> Fillet001
FEATURE [Sketcher::SketchObject] Sketch009
  ArcFitTolerance = 1e-06
  AttachmentSupport = -> [Pad]
  FullyConstrained = true
  MakeInternals = false
  MapMode = 5
  Placement = pos=(0,0,6) rot=(0,0,1;0rad)
  sketch-geometry (5):
    g0: LineSegment StartX=46 StartY=-26 StartZ=0 EndX=46 EndY=26 EndZ=0
    g1: LineSegment StartX=46 StartY=26 StartZ=0 EndX=-46 EndY=26 EndZ=0
    g2: LineSegment StartX=-46 StartY=26 StartZ=0 EndX=-46 EndY=-26 EndZ=0
    g3: LineSegment StartX=-46 StartY=-26 StartZ=0 EndX=46 EndY=-26 EndZ=0
    g4: GeomPoint [constr] X=0 Y=0 Z=0
  constraints (12):
    c: Coincident(g0,g1)
    c: Coincident(g1,g2)
    c: Coincident(g2,g3)
    c: Coincident(g3,g0)
    c: Vertical(g0)
    c: Vertical(g2)
    c: Horizontal(g1)
    c: Horizontal(g3)
    c: Symmetric(g2,g0,g4)
    c: Coincident(g4,g-1)
    c: DistanceX(g1,g1) = 92
    c: DistanceY(g0,g0) = 52
FEATURE [PartDesign::Pocket] Pocket
  BaseFeature = -> Pad
  Direction = (0,0,-1)
  Length = 0.9
  Length2 = 5
  Profile = -> Sketch009
  ReferenceAxis = -> Sketch009 [N_Axis]
  Refine = true
  Suppressed = false
  Type = 0
FEATURE [PartDesign::Body] Body  label="Face"
  AllowCompound = false
  Group = -> [Sketch,Pad,Sketch009,Pocket]
  Origin = -> Origin
  Placement = pos=(0,0,19.4) rot=(0,0,1;0rad)
  Tip = -> Pocket
FEATURE [Sketcher::SketchObject] Sketch010
  ArcFitTolerance = 1e-06
  AttachmentSupport = -> [XY_Plane003]
  FullyConstrained = true
  MakeInternals = false
  MapMode = 5
  sketch-geometry (5):
    g0: LineSegment StartX=49 StartY=-29.5 StartZ=0 EndX=49 EndY=29.5 EndZ=0
    g1: LineSegment StartX=49 StartY=29.5 StartZ=0 EndX=-49 EndY=29.5 EndZ=0
    g2: LineSegment StartX=-49 StartY=29.5 StartZ=0 EndX=-49 EndY=-29.5 EndZ=0
    g3: LineSegment StartX=-49 StartY=-29.5 StartZ=0 EndX=49 EndY=-29.5 EndZ=0
    g4: GeomPoint [constr] X=0 Y=0 Z=0
  constraints (12):
    c: Coincident(g0,g1)
    c: Coincident(g1,g2)
    c: Coincident(g2,g3)
    c: Coincident(g3,g0)
    c: Vertical(g0)
    c: Vertical(g2)
    c: Horizontal(g1)
    c: Horizontal(g3)
    c: Symmetric(g2,g0,g4)
    c: Coincident(g4,g-1)
    c: DistanceX(g1,g1) = 98
    c: DistanceY(g0,g0) = 59
FEATURE [PartDesign::Pad] Pad007
  Direction = (0,0,1)
  Length = 25
  Length2 = 10
  Profile = -> Sketch010
  ReferenceAxis = -> Sketch010 [N_Axis]
  Refine = true
  Suppressed = false
  Type = 0
FEATURE [Sketcher::SketchObject] Sketch011
  ArcFitTolerance = 1e-06
  AttachmentSupport = -> [Pad007]
  FullyConstrained = true
  MakeInternals = false
  MapMode = 5
  Placement = pos=(0,0,25) rot=(0,0,1;0rad)
  sketch-geometry (5):
    g0: LineSegment StartX=47.5 StartY=-28 StartZ=0 EndX=47.5 EndY=28 EndZ=0
    g1: LineSegment StartX=47.5 StartY=28 StartZ=0 EndX=-47.5 EndY=28 EndZ=0
    g2: LineSegment StartX=-47.5 StartY=28 StartZ=0 EndX=-47.5 EndY=-28 EndZ=0
    g3: LineSegment StartX=-47.5 StartY=-28 StartZ=0 EndX=47.5 EndY=-28 EndZ=0
    g4: GeomPoint [constr] X=0 Y=0 Z=0
  constraints (12):
    c: Coincident(g0,g1)
    c: Coincident(g1,g2)
    c: Coincident(g2,g3)
    c: Coincident(g3,g0)
    c: Vertical(g0)
    c: Vertical(g2)
    c: Horizontal(g1)
    c: Horizontal(g3)
    c: Symmetric(g2,g0,g4)
    c: Coincident(g4,g-1)
    c: DistanceX(g1,g1) = 95
    c: DistanceY(g0,g0) = 56
FEATURE [PartDesign::Pocket] Pocket002
  BaseFeature = -> Pad007
  Direction = (0,0,-1)
  Length = 22
  Length2 = 5
  Profile = -> Sketch011
  ReferenceAxis = -> Sketch011 [N_Axis]
  Refine = true
  Suppressed = false
  Type = 0
FEATURE [Sketcher::SketchObject] Sketch012
  ArcFitTolerance = 1e-06
  AttachmentSupport = -> [Pocket002]
  ExternalGeometry = -> [Pocket002]
  FullyConstrained = true
  MakeInternals = false
  MapMode = 5
  Placement = pos=(-47.5,0,0) rot=(0.57735,0.57735,0.57735;2.0944rad)
  sketch-geometry (4):
    g0: LineSegment StartX=-28 StartY=15.5 StartZ=0 EndX=-28 EndY=13.5 EndZ=0
    g1: LineSegment StartX=-28 StartY=13.5 StartZ=0 EndX=28 EndY=13.5 EndZ=0
    g2: LineSegment StartX=28 StartY=13.5 StartZ=0 EndX=28 EndY=15.5 EndZ=0
    g3: LineSegment StartX=28 StartY=15.5 StartZ=0 EndX=-28 EndY=15.5 EndZ=0
  constraints (12):
    c: Coincident(g0,g1)
    c: Coincident(g1,g2)
    c: Coincident(g2,g3)
    c: Coincident(g3,g0)
    c: Vertical(g0)
    c: Vertical(g2)
    c: Horizontal(g1)
    c: Horizontal(g3)
    c: PointOnObject(g0,g-6)
    c: PointOnObject(g1,g-7)
    c: DistanceY(g0,g-6) = 9.5
    c: DistanceY(g0,g0) = 2
FEATURE [PartDesign::Pad] Pad008
  BaseFeature = -> Pocket002
  Direction = (1,0,0)
  Length = 1
  Length2 = 10
  Profile = -> Sketch012
  ReferenceAxis = -> Sketch012 [N_Axis]
  Refine = true
  Suppressed = false
  Type = 0
FEATURE [Sketcher::SketchObject] Sketch013
  ArcFitTolerance = 1e-06
  AttachmentSupport = -> [Pad008]
  ExternalGeometry = -> [Pad008]
  FullyConstrained = false
  MakeInternals = false
  MapMode = 5
  Placement = pos=(47.5,0,0) rot=(0.57735,-0.57735,-0.57735;2.0944rad)
  sketch-geometry (4):
    g0: LineSegment StartX=-28 StartY=15.5 StartZ=0 EndX=-28 EndY=13.5 EndZ=0
    g1: LineSegment StartX=-28 StartY=13.5 StartZ=0 EndX=28.0252 EndY=13.5 EndZ=0
    g2: LineSegment StartX=28.0252 StartY=13.5 StartZ=0 EndX=28.0252 EndY=15.5 EndZ=0
    g3: LineSegment StartX=28.0252 StartY=15.5 StartZ=0 EndX=-28 EndY=15.5 EndZ=0
  constraints (11):
    c: Coincident(g0,g1)
    c: Coincident(g1,g2)
    c: Coincident(g2,g3)
    c: Coincident(g3,g0)
    c: Vertical(g0)
    c: Vertical(g2)
    c: Horizontal(g1)
    c: Horizontal(g3)
    c: PointOnObject(g0,g-5)
    c: DistanceY(g0,g-5) = 9.5
    c: DistanceY(g0,g0) = 2
FEATURE [PartDesign::Pad] Pad009
  BaseFeature = -> Pad008
  Direction = (-1,0,0)
  Length = 1
  Length2 = 10
  Profile = -> Sketch013
  ReferenceAxis = -> Sketch013 [N_Axis]
  Refine = true
  Suppressed = false
  Type = 0
FEATURE [Sketcher::SketchObject] Sketch014
  ArcFitTolerance = 1e-06
  AttachmentSupport = -> [Pad009]
  ExternalGeometry = -> [Pad009]
  FullyConstrained = true
  MakeInternals = false
  MapMode = 5
  Placement = pos=(0,0,3) rot=(0,0,1;0rad)
FEATURE [Sketcher::SketchObject] Sketch015
  ArcFitTolerance = 1e-06
  AttachmentSupport = -> [Pad009]
  ExternalGeometry = -> [Pad009]
  FullyConstrained = true
  MakeInternals = false
  MapMode = 5
  Placement = pos=(49,0,0) rot=(0.57735,0.57735,0.57735;2.0944rad)
  sketch-geometry (4):
    g0: LineSegment StartX=-27.5 StartY=1.5 StartZ=0 EndX=-26.75 EndY=5 EndZ=0
    g1: LineSegment StartX=-26.75 StartY=5 StartZ=0 EndX=-5.75 EndY=5 EndZ=0
    g2: LineSegment StartX=-5.75 StartY=5 StartZ=0 EndX=-5 EndY=1.5 EndZ=0
    g3: LineSegment StartX=-5 StartY=1.5 StartZ=0 EndX=-27.5 EndY=1.5 EndZ=0
  constraints (12):
    c: Coincident(g0,g1)
    c: Horizontal(g1)
    c: Coincident(g1,g2)
    c: DistanceY(g-3,g0) = 1.5
    c: DistanceY(g0,g0) = 3.5
    c: DistanceX(g0,g2) = 22.5
    c: DistanceY(g-3,g2) = 1.5
    c: Coincident(g2,g3)
    c: Coincident(g3,g0)
    c: DistanceX(g-3,g0) = 2
    c: DistanceX(g1,g1) = 21
    c: DistanceX(g0,g0) = 0.75
FEATURE [PartDesign::Pocket] Pocket003
  BaseFeature = -> Pad009
  Direction = (-1,0,0)
  Length = 53
  Length2 = 5
  Profile = -> Sketch015
  ReferenceAxis = -> Sketch015 [N_Axis]
  Refine = true
  Suppressed = false
  Type = 0
FEATURE [Mesh::Feature] PicoW
  Placement = pos=(-4,-6,5.8) rot=(0,0,-1;1.5708rad)
FEATURE [Sketcher::SketchObject] Sketch017
  ArcFitTolerance = 1e-06
  AttachmentSupport = -> [Pocket003]
  FullyConstrained = false
  MakeInternals = false
  MapMode = 5
  Placement = pos=(0,0,1.5) rot=(0,0,1;0rad)
  sketch-geometry (2):
    g0: Circle CenterX=-2.01146 CenterY=-10.801 CenterZ=0 NormalX=0 NormalY=0 NormalZ=1 AngleXU=0 Radius=0.869454
    g1: Circle CenterX=-2.01146 CenterY=-22.2013 CenterZ=0 NormalX=0 NormalY=0 NormalZ=1 AngleXU=0 Radius=0.804164
  constraints (1):
    c: DistanceX(g1,g0) = 0
FEATURE [PartDesign::Pad] Pad010
  BaseFeature = -> Pocket003
  Direction = (0,0,1)
  Length = 1
  Length2 = 10
  Profile = -> Sketch017
  ReferenceAxis = -> Sketch017 [N_Axis]
  Refine = true
  Suppressed = false
  Type = 0
FEATURE [PartDesign::Body] Body003  label="Case v2"
  AllowCompound = false
  Group = -> [Sketch010,Pad007,Sketch011,Pocket002,Sketch012,Pad008,Sketch013,Pad009,Sketch014,Sketch015,Pocket003,Sketch017,Pad010]
  Origin = -> Origin003
  Tip = -> Pad010
FEATURE [Sketcher::SketchObject] Sketch018
  ArcFitTolerance = 1e-06
  AttachmentSupport = -> [XY_Plane004]
  FullyConstrained = true
  MakeInternals = false
  MapMode = 5
  sketch-geometry (5):
    g0: LineSegment StartX=-26 StartY=-10 StartZ=0 EndX=26 EndY=-10 EndZ=0
    g1: LineSegment StartX=26 StartY=-10 StartZ=0 EndX=26 EndY=10 EndZ=0
    g2: LineSegment StartX=26 StartY=10 StartZ=0 EndX=-26 EndY=10 EndZ=0
    g3: LineSegment StartX=-26 StartY=10 StartZ=0 EndX=-26 EndY=-10 EndZ=0
    g4: GeomPoint [constr] X=0 Y=0 Z=0
  constraints (12):
    c: Coincident(g0,g1)
    c: Coincident(g1,g2)
    c: Coincident(g2,g3)
    c: Coincident(g3,g0)
    c: Horizontal(g0)
    c: Horizontal(g2)
    c: Vertical(g1)
    c: Vertical(g3)
    c: Symmetric(g2,g0,g4)
    c: Coincident(g4,g-1)
    c: DistanceX(g2,g2) = 52
    c: DistanceY(g1,g1) = 20
FEATURE [PartDesign::Pad] Pad011
  Direction = (0,0,1)
  Length = 2
  Length2 = 10
  Profile = -> Sketch018
  ReferenceAxis = -> Sketch018 [N_Axis]
  Refine = true
  Suppressed = false
  Type = 0
FEATURE [Sketcher::SketchObject] Sketch020
  ArcFitTolerance = 1e-06
  AttachmentSupport = -> [Pad011]
  ExternalGeometry = -> [Pad011]
  FullyConstrained = true
  MakeInternals = false
  MapMode = 5
  Placement = pos=(0,0,2) rot=(0,0,1;0rad)
  sketch-geometry (4):
    g0: Circle CenterX=-23.5 CenterY=5.7 CenterZ=0 NormalX=0 NormalY=0 NormalZ=1 AngleXU=0 Radius=1.75
    g1: Circle CenterX=-23.5 CenterY=-5.7 CenterZ=0 NormalX=0 NormalY=0 NormalZ=1 AngleXU=0 Radius=1.75
    g2: Circle CenterX=23.5 CenterY=-5.7 CenterZ=0 NormalX=0 NormalY=0 NormalZ=1 AngleXU=0 Radius=1.75
    g3: Circle CenterX=23.5 CenterY=5.7 CenterZ=0 NormalX=0 NormalY=0 NormalZ=1 AngleXU=0 Radius=1.75
  constraints (12):
    c: DistanceY(g3,g0) = 0
    c: DistanceX(g3,g2) = 0
    c: DistanceY(g1,g2) = 0
    c: DistanceX(g0,g1) = 0
    c: DistanceY(g1,g0) = 11.4
    c: DistanceX(g1,g2) = 47
    c: DistanceX(g-3,g0) = 2.5
    c: DistanceY(g0,g-5) = 4.3
    c: Equal(g0,g1)
    c: Equal(g1,g2)
    c: Equal(g2,g3)
    c: Diameter(g0) = 3.5
FEATURE [PartDesign::Pad] Pad012
  BaseFeature = -> Pad011
  Direction = (0,0,1)
  Length = 2
  Length2 = 10
  Profile = -> Sketch020
  ReferenceAxis = -> Sketch020 [N_Axis]
  Refine = true
  Suppressed = false
  Type = 0
FEATURE [PartDesign::Fillet] Fillet002
  Base = -> Pad012 [Edge13,Edge15,Edge16,Edge14]
  BaseFeature = -> Pad012
  Radius = 1.9
  Refine = true
  SupportTransform = false
  Suppressed = false
  UseAllEdges = false
FEATURE [Sketcher::SketchObject] Sketch021
  ArcFitTolerance = 1e-06
  AttachmentSupport = -> [Fillet002]
  FullyConstrained = true
  MakeInternals = false
  MapMode = 5
  Placement = pos=(0,0,4) rot=(0,0,1;0rad)
  sketch-geometry (4):
    g0: Circle CenterX=-23.53 CenterY=5.71 CenterZ=0 NormalX=0 NormalY=0 NormalZ=1 AngleXU=0 Radius=1
    g1: Circle CenterX=-23.53 CenterY=-5.71 CenterZ=0 NormalX=0 NormalY=0 NormalZ=1 AngleXU=0 Radius=1
    g2: Circle CenterX=23.47 CenterY=-5.71 CenterZ=0 NormalX=0 NormalY=0 NormalZ=1 AngleXU=0 Radius=1
    g3: Circle CenterX=23.47 CenterY=5.73 CenterZ=0 NormalX=0 NormalY=0 NormalZ=1 AngleXU=0 Radius=1
  constraints (12):
    c: DistanceX(g3,g2) = 0
    c: DistanceY(g2,g3) = 11.44
    c: DistanceY(g1,g2) = 0
    c: DistanceX(g1,g0) = 0
    c: DistanceX(g0,g3) = 47
    c: DistanceY(g1,g0) = 11.42
    c: DistanceY(g-1,g0) = 5.71
    c: DistanceX(g0,g-1) = 23.53
    c: Equal(g0,g1)
    c: Equal(g1,g2)
    c: Equal(g2,g3)
    c: Diameter(g0) = 2
FEATURE [PartDesign::Hole] Hole
  BaseFeature = -> Fillet002
  CustomThreadClearance = 0
  Depth = 2
  DepthType = 0
  Diameter = 2
  DrillForDepth = false
  DrillPoint = 0
  DrillPointAngle = 118
  HoleCutCountersinkAngle = 90
  HoleCutCustomValues = false
  HoleCutDepth = 0
  HoleCutDiameter = 6.1
  HoleCutType = 0
  ModelThread = false
  Profile = -> Sketch021
  Refine = true
  Suppressed = false
  Tapered = true
  TaperedAngle = 87
  ThreadClass = 0
  ThreadDepth = 2
  ThreadDepthType = 0
  ThreadDirection = 0
  ThreadFit = 0
  ThreadSize = 0
  ThreadType = 0
  Threaded = false
  UseCustomThreadClearance = false
FEATURE [PartDesign::Body] Body004  label="pico sled"
  AllowCompound = false
  Group = -> [Sketch018,Pad011,Sketch020,Pad012,Fillet002,Sketch021,Hole]
  Origin = -> Origin004
  Placement = pos=(23.8,-18,2.1) rot=(0,0,1;0rad)
  Tip = -> Hole
FEATURE [Sketcher::SketchObject] Sketch022
  ArcFitTolerance = 1e-06
  AttachmentSupport = -> [XY_Plane005]
  FullyConstrained = true
  MakeInternals = false
  MapMode = 5
  sketch-geometry (5):
    g0: LineSegment StartX=-50 StartY=-30.5 StartZ=0 EndX=50 EndY=-30.5 EndZ=0
    g1: LineSegment StartX=50 StartY=-30.5 StartZ=0 EndX=50 EndY=30.5 EndZ=0
    g2: LineSegment StartX=50 StartY=30.5 StartZ=0 EndX=-50 EndY=30.5 EndZ=0
    g3: LineSegment StartX=-50 StartY=30.5 StartZ=0 EndX=-50 EndY=-30.5 EndZ=0
    g4: GeomPoint [constr] X=0 Y=0 Z=0
  constraints (12):
    c: Coincident(g0,g1)
    c: Coincident(g1,g2)
    c: Coincident(g2,g3)
    c: Coincident(g3,g0)
    c: Horizontal(g0)
    c: Horizontal(g2)
    c: Vertical(g1)
    c: Vertical(g3)
    c: Symmetric(g2,g0,g4)
    c: Coincident(g4,g-1)
    c: DistanceX(g2,g2) = 100
    c: DistanceY(g1,g1) = 61
FEATURE [PartDesign::Pad] Pad013
  Direction = (0,0,1)
  Length = 30
  Length2 = 10
  Profile = -> Sketch022
  ReferenceAxis = -> Sketch022 [N_Axis]
  Refine = true
  Suppressed = false
  Type = 0
FEATURE [Sketcher::SketchObject] Sketch023
  ArcFitTolerance = 1e-06
  AttachmentSupport = -> [Pad013]
  FullyConstrained = true
  MakeInternals = false
  MapMode = 5
  Placement = pos=(0,0,30) rot=(0,0,1;0rad)
  sketch-geometry (5):
    g0: LineSegment StartX=47.5 StartY=-28 StartZ=0 EndX=47.5 EndY=28 EndZ=0
    g1: LineSegment StartX=47.5 StartY=28 StartZ=0 EndX=-47.5 EndY=28 EndZ=0
    g2: LineSegment StartX=-47.5 StartY=28 StartZ=0 EndX=-47.5 EndY=-28 EndZ=0
    g3: LineSegment StartX=-47.5 StartY=-28 StartZ=0 EndX=47.5 EndY=-28 EndZ=0
    g4: GeomPoint [constr] X=0 Y=0 Z=0
  constraints (12):
    c: Coincident(g0,g1)
    c: Coincident(g1,g2)
    c: Coincident(g2,g3)
    c: Coincident(g3,g0)
    c: Vertical(g0)
    c: Vertical(g2)
    c: Horizontal(g1)
    c: Horizontal(g3)
    c: Symmetric(g2,g0,g4)
    c: Coincident(g4,g-1)
    c: DistanceX(g1,g1) = 95
    c: DistanceY(g2,g2) = 56
FEATURE [PartDesign::Pocket] Pocket004
  BaseFeature = -> Pad013
  Direction = (0,0,-1)
  Length = 25
  Length2 = 5
  Profile = -> Sketch023
  ReferenceAxis = -> Sketch023 [N_Axis]
  Refine = true
  Suppressed = false
  Type = 0
FEATURE [Sketcher::SketchObject] Sketch024
  ArcFitTolerance = 1e-06
  AttachmentSupport = -> [Pocket004]
  ExternalGeometry = -> [Pocket004]
  FullyConstrained = true
  MakeInternals = false
  MapMode = 5
  Placement = pos=(50,0,0) rot=(0.57735,0.57735,0.57735;2.0944rad)
  sketch-geometry (4):
    g0: LineSegment StartX=-28 StartY=11.5 StartZ=0 EndX=-28 EndY=2 EndZ=0
    g1: LineSegment StartX=-28 StartY=2 StartZ=0 EndX=-8 EndY=2 EndZ=0
    g2: LineSegment StartX=-8 StartY=2 StartZ=0 EndX=-8 EndY=11.5 EndZ=0
    g3: LineSegment StartX=-8 StartY=11.5 StartZ=0 EndX=-28 EndY=11.5 EndZ=0
  constraints (12):
    c: Coincident(g0,g1)
    c: Coincident(g1,g2)
    c: Coincident(g2,g3)
    c: Coincident(g3,g0)
    c: Vertical(g0)
    c: Vertical(g2)
    c: Horizontal(g1)
    c: Horizontal(g3)
    c: DistanceX(g3,g3) = 20
    c: DistanceY(g2,g2) = 9.5
    c: DistanceY(g-1,g1) = 2
    c: DistanceX(g0,g-4) = 0
FEATURE [PartDesign::Pocket] Pocket005
  BaseFeature = -> Pocket004
  Direction = (-1,0,0)
  Length = 2.5
  Length2 = 5
  Profile = -> Sketch024
  ReferenceAxis = -> Sketch024 [N_Axis]
  Refine = true
  Suppressed = false
  Type = 0
FEATURE [Sketcher::SketchObject] Sketch025
  ArcFitTolerance = 1e-06
  AttachmentSupport = -> [Pocket005]
  ExternalGeometry = -> [Pocket005]
  FullyConstrained = true
  MakeInternals = false
  MapMode = 5
  Placement = pos=(47.5,0,0) rot=(0.57735,0.57735,0.57735;2.0944rad)
  sketch-geometry (4):
    g0: LineSegment StartX=-28 StartY=2 StartZ=0 EndX=-8 EndY=2 EndZ=0
    g1: LineSegment StartX=-8 StartY=2 StartZ=0 EndX=-8 EndY=4.5 EndZ=0
    g2: LineSegment StartX=-8 StartY=4.5 StartZ=0 EndX=-28 EndY=4.5 EndZ=0
    g3: LineSegment StartX=-28 StartY=4.5 StartZ=0 EndX=-28 EndY=2 EndZ=0
  constraints (12):
    c: Coincident(g0,g1)
    c: Coincident(g1,g2)
    c: Coincident(g2,g3)
    c: Coincident(g3,g0)
    c: Horizontal(g0)
    c: Horizontal(g2)
    c: Vertical(g1)
    c: Vertical(g3)
    c: DistanceX(g-3,g2) = 0
    c: DistanceX(g1,g-4) = 0
    c: DistanceY(g3,g3) = 2.5
    c: DistanceY(g-3,g0) = 0
FEATURE [PartDesign::Pocket] Pocket006
  BaseFeature = -> Pocket005
  Direction = (-1,0,0)
  Length = 50
  Length2 = 5
  Profile = -> Sketch025
  ReferenceAxis = -> Sketch025 [N_Axis]
  Refine = true
  Suppressed = false
  Type = 0
FEATURE [Sketcher::SketchObject] Sketch026
  ArcFitTolerance = 1e-06
  AttachmentSupport = -> [Pocket006]
  ExternalGeometry = -> [Pocket006]
  FullyConstrained = true
  MakeInternals = false
  MapMode = 5
  Placement = pos=(47.5,0,0) rot=(0.57735,0.57735,0.57735;2.0944rad)
  sketch-geometry (4):
    g0: LineSegment StartX=-26.5 StartY=5 StartZ=0 EndX=-26.5 EndY=4.5 EndZ=0
    g1: LineSegment StartX=-26.5 StartY=4.5 StartZ=0 EndX=-9.5 EndY=4.5 EndZ=0
    g2: LineSegment StartX=-9.5 StartY=4.5 StartZ=0 EndX=-9.5 EndY=5 EndZ=0
    g3: LineSegment StartX=-9.5 StartY=5 StartZ=0 EndX=-26.5 EndY=5 EndZ=0
  constraints (12):
    c: Coincident(g0,g1)
    c: Coincident(g1,g2)
    c: Coincident(g2,g3)
    c: Coincident(g3,g0)
    c: Vertical(g0)
    c: Vertical(g2)
    c: Horizontal(g1)
    c: Horizontal(g3)
    c: PointOnObject(g0,g-3)
    c: PointOnObject(g1,g-4)
    c: DistanceX(g3,g3) = 17
    c: DistanceX(g-4,g0) = 1.5
FEATURE [PartDesign::Pocket] Pocket007
  BaseFeature = -> Pocket006
  Direction = (-1,0,0)
  Length = 50
  Length2 = 5
  Profile = -> Sketch026
  ReferenceAxis = -> Sketch026 [N_Axis]
  Refine = true
  Suppressed = false
  Type = 0
FEATURE [PartDesign::Body] Body005  label="Case v3"
  AllowCompound = false
  Group = -> [Sketch022,Pad013,Sketch023,Pocket004,Sketch024,Pocket005,Sketch025,Pocket006,Sketch026,Pocket007]
  Origin = -> Origin005
  Tip = -> Pocket007
FEATURE [Sketcher::SketchObject] Sketch027
  ArcFitTolerance = 1e-06
  AttachmentSupport = -> [XY_Plane006]
  FullyConstrained = true
  MakeInternals = false
  MapMode = 5
  sketch-geometry (5):
    g0: LineSegment StartX=49 StartY=-29.5 StartZ=0 EndX=49 EndY=29.5 EndZ=0
    g1: LineSegment StartX=49 StartY=29.5 StartZ=0 EndX=-49 EndY=29.5 EndZ=0
    g2: LineSegment StartX=-49 StartY=29.5 StartZ=0 EndX=-49 EndY=-29.5 EndZ=0
    g3: LineSegment StartX=-49 StartY=-29.5 StartZ=0 EndX=49 EndY=-29.5 EndZ=0
    g4: GeomPoint [constr] X=0 Y=0 Z=0
  constraints (12):
    c: Coincident(g0,g1)
    c: Coincident(g1,g2)
    c: Coincident(g2,g3)
    c: Coincident(g3,g0)
    c: Vertical(g0)
    c: Vertical(g2)
    c: Horizontal(g1)
    c: Horizontal(g3)
    c: Symmetric(g2,g0,g4)
    c: Coincident(g4,g-1)
    c: DistanceX(g1,g1) = 98
    c: DistanceY(g0,g0) = 59
FEATURE [PartDesign::Pad] Pad014
  Direction = (0,0,1)
  Length = 25
  Length2 = 10
  Profile = -> Sketch027
  ReferenceAxis = -> Sketch027 [N_Axis]
  Refine = true
  Suppressed = false
  Type = 0
FEATURE [Sketcher::SketchObject] Sketch028
  ArcFitTolerance = 1e-06
  AttachmentSupport = -> [Pad014]
  FullyConstrained = true
  MakeInternals = false
  MapMode = 5
  Placement = pos=(0,0,25) rot=(0,0,1;0rad)
  sketch-geometry (5):
    g0: LineSegment StartX=47.5 StartY=-28 StartZ=0 EndX=47.5 EndY=28 EndZ=0
    g1: LineSegment StartX=47.5 StartY=28 StartZ=0 EndX=-47.5 EndY=28 EndZ=0
    g2: LineSegment StartX=-47.5 StartY=28 StartZ=0 EndX=-47.5 EndY=-28 EndZ=0
    g3: LineSegment StartX=-47.5 StartY=-28 StartZ=0 EndX=47.5 EndY=-28 EndZ=0
    g4: GeomPoint [constr] X=0 Y=0 Z=0
  constraints (12):
    c: Coincident(g0,g1)
    c: Coincident(g1,g2)
    c: Coincident(g2,g3)
    c: Coincident(g3,g0)
    c: Vertical(g0)
    c: Vertical(g2)
    c: Horizontal(g1)
    c: Horizontal(g3)
    c: Symmetric(g2,g0,g4)
    c: Coincident(g4,g-1)
    c: DistanceX(g1,g1) = 95
    c: DistanceY(g0,g0) = 56
FEATURE [PartDesign::Pocket] Pocket008
  BaseFeature = -> Pad014
  Direction = (0,0,-1)
  Length = 22
  Length2 = 5
  Profile = -> Sketch028
  ReferenceAxis = -> Sketch028 [N_Axis]
  Refine = true
  Suppressed = false
  Type = 0
FEATURE [Sketcher::SketchObject] Sketch029
  ArcFitTolerance = 1e-06
  AttachmentSupport = -> [Pocket008]
  ExternalGeometry = -> [Pocket008]
  FullyConstrained = true
  MakeInternals = false
  MapMode = 5
  Placement = pos=(-47.5,0,0) rot=(0.57735,0.57735,0.57735;2.0944rad)
  sketch-geometry (4):
    g0: LineSegment StartX=-28 StartY=15.5 StartZ=0 EndX=-28 EndY=13.5 EndZ=0
    g1: LineSegment StartX=-28 StartY=13.5 StartZ=0 EndX=28 EndY=13.5 EndZ=0
    g2: LineSegment StartX=28 StartY=13.5 StartZ=0 EndX=28 EndY=15.5 EndZ=0
    g3: LineSegment StartX=28 StartY=15.5 StartZ=0 EndX=-28 EndY=15.5 EndZ=0
  constraints (12):
    c: Coincident(g0,g1)
    c: Coincident(g1,g2)
    c: Coincident(g2,g3)
    c: Coincident(g3,g0)
    c: Vertical(g0)
    c: Vertical(g2)
    c: Horizontal(g1)
    c: Horizontal(g3)
    c: PointOnObject(g0,g-6)
    c: PointOnObject(g1,g-7)
    c: DistanceY(g0,g-6) = 9.5
    c: DistanceY(g0,g0) = 2
FEATURE [PartDesign::Pad] Pad015
  BaseFeature = -> Pocket008
  Direction = (1,0,0)
  Length = 1
  Length2 = 10
  Profile = -> Sketch029
  ReferenceAxis = -> Sketch029 [N_Axis]
  Refine = true
  Suppressed = false
  Type = 0
FEATURE [Sketcher::SketchObject] Sketch030
  ArcFitTolerance = 1e-06
  AttachmentSupport = -> [Pad015]
  ExternalGeometry = -> [Pad015]
  FullyConstrained = false
  MakeInternals = false
  MapMode = 5
  Placement = pos=(47.5,0,0) rot=(0.57735,-0.57735,-0.57735;2.0944rad)
  sketch-geometry (4):
    g0: LineSegment StartX=-28 StartY=15.5 StartZ=0 EndX=-28 EndY=13.5 EndZ=0
    g1: LineSegment StartX=-28 StartY=13.5 StartZ=0 EndX=28.0252 EndY=13.5 EndZ=0
    g2: LineSegment StartX=28.0252 StartY=13.5 StartZ=0 EndX=28.0252 EndY=15.5 EndZ=0
    g3: LineSegment StartX=28.0252 StartY=15.5 StartZ=0 EndX=-28 EndY=15.5 EndZ=0
  constraints (11):
    c: Coincident(g0,g1)
    c: Coincident(g1,g2)
    c: Coincident(g2,g3)
    c: Coincident(g3,g0)
    c: Vertical(g0)
    c: Vertical(g2)
    c: Horizontal(g1)
    c: Horizontal(g3)
    c: PointOnObject(g0,g-5)
    c: DistanceY(g0,g-5) = 9.5
    c: DistanceY(g0,g0) = 2
FEATURE [PartDesign::Pad] Pad016
  BaseFeature = -> Pad015
  Direction = (-1,0,0)
  Length = 1
  Length2 = 10
  Profile = -> Sketch030
  ReferenceAxis = -> Sketch030 [N_Axis]
  Refine = true
  Suppressed = false
  Type = 0
FEATURE [Sketcher::SketchObject] Sketch031
  ArcFitTolerance = 1e-06
  AttachmentSupport = -> [Pad016]
  FullyConstrained = true
  MakeInternals = false
  MapMode = 5
  Placement = pos=(0,0,3) rot=(0,0,1;0rad)
  sketch-geometry (4):
    g0: Circle CenterX=-2 CenterY=-10.78 CenterZ=0 NormalX=0 NormalY=0 NormalZ=1 AngleXU=0 Radius=1.75
    g1: Circle CenterX=45 CenterY=-10.78 CenterZ=0 NormalX=0 NormalY=0 NormalZ=1 AngleXU=0 Radius=1.75
    g2: Circle CenterX=45 CenterY=-22.21 CenterZ=0 NormalX=0 NormalY=0 NormalZ=1 AngleXU=0 Radius=1.75
    g3: Circle CenterX=-2 CenterY=-22.21 CenterZ=0 NormalX=0 NormalY=0 NormalZ=1 AngleXU=0 Radius=1.75
  constraints (12):
    c: Equal(g1,g2)
    c: Equal(g2,g3)
    c: Equal(g3,g0)
    c: DistanceX(g3,g0) = 0
    c: DistanceX(g2,g1) = 0
    c: DistanceY(g2,g3) = 0
    c: DistanceY(g0,g1) = 0
    c: Diameter(g0) = 3.5
    c: DistanceY(g3,g0) = 11.43
    c: DistanceX(g3,g2) = 47
    c: DistanceY(g0,g-1) = 10.78
    c: DistanceX(g0,g-1) = 2
FEATURE [PartDesign::Pad] Pad017
  BaseFeature = -> Pad016
  Direction = (0,0,1)
  Length = 2
  Length2 = 10
  Profile = -> Sketch031
  ReferenceAxis = -> Sketch031 [N_Axis]
  Refine = true
  Suppressed = false
  Type = 0
FEATURE [Sketcher::SketchObject] Sketch032
  ArcFitTolerance = 1e-06
  AttachmentSupport = -> [Pad017]
  FullyConstrained = true
  MakeInternals = false
  MapMode = 5
  Placement = pos=(0,0,5) rot=(0,0,1;0rad)
  sketch-geometry (4):
    g0: Circle CenterX=-2.01 CenterY=-10.76 CenterZ=0 NormalX=0 NormalY=0 NormalZ=1 AngleXU=0 Radius=0.95
    g1: Circle CenterX=-2.01 CenterY=-22.21 CenterZ=0 NormalX=0 NormalY=0 NormalZ=1 AngleXU=0 Radius=0.95
    g2: Circle CenterX=44.95 CenterY=-22.21 CenterZ=0 NormalX=0 NormalY=0 NormalZ=1 AngleXU=0 Radius=0.95
    g3: Circle CenterX=44.95 CenterY=-10.76 CenterZ=0 NormalX=0 NormalY=0 NormalZ=1 AngleXU=0 Radius=0.95
  constraints (12):
    c: Equal(g0,g1)
    c: Equal(g1,g2)
    c: Equal(g2,g3)
    c: DistanceX(g0,g1) = 0
    c: DistanceY(g3,g0) = 0
    c: DistanceY(g1,g2) = 0
    c: DistanceX(g2,g3) = 0
    c: Diameter(g0) = 1.9
    c: DistanceX(g0,g3) = 46.96
    c: DistanceY(g1,g0) = 11.45
    c: DistanceX(g0,g-1) = 2.01
    c: DistanceY(g0,g-1) = 10.76
FEATURE [PartDesign::Pocket] Pocket009
  BaseFeature = -> Pad017
  Direction = (0,0,-1)
  Length = 3
  Length2 = 5
  Profile = -> Sketch032
  ReferenceAxis = -> Sketch032 [N_Axis]
  Refine = true
  Suppressed = false
  Type = 0
FEATURE [PartDesign::Fillet] Fillet003
  Base = -> Pocket009 [Edge49,Edge47,Edge50,Edge48]
  BaseFeature = -> Pocket009
  Radius = 1.9
  Refine = true
  SupportTransform = false
  Suppressed = false
  UseAllEdges = false
FEATURE [Sketcher::SketchObject] Sketch033
  ArcFitTolerance = 1e-06
  AttachmentSupport = -> [Fillet003]
  ExternalGeometry = -> [Fillet003]
  FullyConstrained = false
  MakeInternals = false
  MapMode = 5
  Placement = pos=(47.5,0,0) rot=(0.57735,-0.57735,-0.57735;2.0944rad)
  sketch-geometry (10):
    g0: LineSegment StartX=8.29325 StartY=7.80927 StartZ=0 EndX=8.29325 EndY=7.7839 EndZ=0
    g1: LineSegment StartX=11.2806 StartY=4.79659 StartZ=0 EndX=21.2806 EndY=4.79659 EndZ=0
    g2: LineSegment StartX=24.2679 StartY=7.7839 StartZ=0 EndX=24.2679 EndY=7.80927 EndZ=0
    g3: LineSegment StartX=21.2806 StartY=10.7966 StartZ=0 EndX=11.2806 EndY=10.7966 EndZ=0
    g4: ArcOfCircle CenterX=11.2806 CenterY=7.80927 CenterZ=0 NormalX=0 NormalY=0 NormalZ=1 AngleXU=0 Radius=2.98732 StartAngle=1.5708 EndAngle=3.14159
    g5: ArcOfCircle CenterX=11.2806 CenterY=7.7839 CenterZ=0 NormalX=0 NormalY=0 NormalZ=1 AngleXU=0 Radius=2.98732 StartAngle=3.14159 EndAngle=4.71239
    g6: ArcOfCircle CenterX=21.2806 CenterY=7.7839 CenterZ=0 NormalX=0 NormalY=0 NormalZ=1 AngleXU=0 Radius=2.98732 StartAngle=4.71239 EndAngle=6.28319
    g7: ArcOfCircle CenterX=21.2806 CenterY=7.80927 CenterZ=0 NormalX=0 NormalY=0 NormalZ=1 AngleXU=0 Radius=2.98732 StartAngle=0 EndAngle=1.5708
    g8: GeomPoint [constr] X=8.29325 Y=10.7966 Z=0
    g9: GeomPoint [constr] X=24.2679 Y=4.79659 Z=0
  constraints (21):
    c: Tangent(g0,g4) = -1.5708
    c: Tangent(g0,g5) = -1.5708
    c: Tangent(g1,g5) = -1.5708
    c: Tangent(g1,g6) = -1.5708
    c: Tangent(g2,g6) = -1.5708
    c: Tangent(g2,g7) = -1.5708
    c: Tangent(g3,g7) = -1.5708
    c: Tangent(g3,g4) = -1.5708
    c: Vertical(g0)
    c: Vertical(g2)
    c: Horizontal(g1)
    c: Horizontal(g3)
    c: Equal(g4,g5)
    c: Equal(g5,g6)
    c: Equal(g6,g7)
    c: PointOnObject(g8,g0)
    c: PointOnObject(g8,g3)
    c: PointOnObject(g9,g1)
    c: PointOnObject(g9,g2)
    c: DistanceX(g3,g3) = 10
    c: DistanceY(g1,g3) = 6
FEATURE [PartDesign::Pocket] Pocket010
  BaseFeature = -> Fillet003
  Direction = (1,0,0)
  Length = 3
  Length2 = 5
  Profile = -> Sketch033
  ReferenceAxis = -> Sketch033 [N_Axis]
  Refine = true
  Suppressed = false
  Type = 0
FEATURE [PartDesign::Fillet] Fillet004
  Base = -> Pocket010 [Edge65,Edge77,Edge75,Edge67,Edge69,Edge73]
  BaseFeature = -> Pocket010
  Radius = 1
  Refine = true
  SupportTransform = false
  Suppressed = false
  UseAllEdges = false
FEATURE [PartDesign::Body] Body006  label="Case v4"
  AllowCompound = false
  Group = -> [Sketch027,Pad014,Sketch028,Pocket008,Sketch029,Pad015,Sketch030,Pad016,Sketch031,Pad017,Sketch032,Pocket009,Fillet003,Sketch033,Pocket010,Fillet004]
  Origin = -> Origin006
  Tip = -> Fillet004
FEATURE [Sketcher::SketchObject] Sketch034
  ArcFitTolerance = 1e-06
  AttachmentSupport = -> [XY_Plane007]
  FullyConstrained = true
  MakeInternals = false
  MapMode = 5
  sketch-geometry (5):
    g0: LineSegment StartX=49 StartY=-29.5 StartZ=0 EndX=49 EndY=29.5 EndZ=0
    g1: LineSegment StartX=49 StartY=29.5 StartZ=0 EndX=-49 EndY=29.5 EndZ=0
    g2: LineSegment StartX=-49 StartY=29.5 StartZ=0 EndX=-49 EndY=-29.5 EndZ=0
    g3: LineSegment StartX=-49 StartY=-29.5 StartZ=0 EndX=49 EndY=-29.5 EndZ=0
    g4: GeomPoint [constr] X=0 Y=0 Z=0
  constraints (12):
    c: Coincident(g0,g1)
    c: Coincident(g1,g2)
    c: Coincident(g2,g3)
    c: Coincident(g3,g0)
    c: Vertical(g0)
    c: Vertical(g2)
    c: Horizontal(g1)
    c: Horizontal(g3)
    c: Symmetric(g2,g0,g4)
    c: Coincident(g4,g-1)
    c: DistanceX(g1,g1) = 98
    c: DistanceY(g0,g0) = 59
FEATURE [PartDesign::Pad] Pad018
  Direction = (0,0,1)
  Length = 25
  Length2 = 10
  Profile = -> Sketch034
  ReferenceAxis = -> Sketch034 [N_Axis]
  Refine = true
  Suppressed = false
  Type = 0
FEATURE [Sketcher::SketchObject] Sketch035
  ArcFitTolerance = 1e-06
  AttachmentSupport = -> [Pad018]
  FullyConstrained = true
  MakeInternals = false
  MapMode = 5
  Placement = pos=(0,0,25) rot=(0,0,1;0rad)
  sketch-geometry (5):
    g0: LineSegment StartX=47.5 StartY=-28 StartZ=0 EndX=47.5 EndY=28 EndZ=0
    g1: LineSegment StartX=47.5 StartY=28 StartZ=0 EndX=-47.5 EndY=28 EndZ=0
    g2: LineSegment StartX=-47.5 StartY=28 StartZ=0 EndX=-47.5 EndY=-28 EndZ=0
    g3: LineSegment StartX=-47.5 StartY=-28 StartZ=0 EndX=47.5 EndY=-28 EndZ=0
    g4: GeomPoint [constr] X=0 Y=0 Z=0
  constraints (12):
    c: Coincident(g0,g1)
    c: Coincident(g1,g2)
    c: Coincident(g2,g3)
    c: Coincident(g3,g0)
    c: Vertical(g0)
    c: Vertical(g2)
    c: Horizontal(g1)
    c: Horizontal(g3)
    c: Symmetric(g2,g0,g4)
    c: Coincident(g4,g-1)
    c: DistanceX(g1,g1) = 95
    c: DistanceY(g0,g0) = 56
FEATURE [PartDesign::Pocket] Pocket011
  BaseFeature = -> Pad018
  Direction = (0,0,-1)
  Length = 22
  Length2 = 5
  Profile = -> Sketch035
  ReferenceAxis = -> Sketch035 [N_Axis]
  Refine = true
  Suppressed = false
  Type = 0
FEATURE [Sketcher::SketchObject] Sketch036
  ArcFitTolerance = 1e-06
  AttachmentSupport = -> [Pocket011]
  FullyConstrained = false
  MakeInternals = false
  MapMode = 5
  Placement = pos=(0,0,3) rot=(0,0,1;0rad)
  sketch-geometry (4):
    g0: Circle CenterX=-14.34 CenterY=0.64 CenterZ=0 NormalX=0 NormalY=0 NormalZ=1 AngleXU=0 Radius=2.5
    g1: Circle CenterX=-14.34 CenterY=23.5354 CenterZ=0 NormalX=0 NormalY=0 NormalZ=1 AngleXU=0 Radius=2.5
    g2: Circle CenterX=43.7012 CenterY=23.5354 CenterZ=0 NormalX=0 NormalY=0 NormalZ=1 AngleXU=0 Radius=2.5
    g3: Circle CenterX=43.7012 CenterY=0.64 CenterZ=0 NormalX=0 NormalY=0 NormalZ=1 AngleXU=0 Radius=2.5
  constraints (10):
    c: Equal(g1,g2)
    c: Equal(g2,g3)
    c: Equal(g3,g0)
    c: Diameter(g1) = 5
    c: Vertical(g1,g0)
    c: Vertical(g3,g2)
    c: Horizontal(g1,g2)
    c: Horizontal(g3,g0)
    c: DistanceX(g0,g-1) = 14.34
    c: DistanceY(g-1,g0) = 0.64
FEATURE [PartDesign::Pad] Pad019
  BaseFeature = -> Pocket011
  Direction = (0,0,1)
  Length = 2
  Length2 = 10
  Profile = -> Sketch036
  ReferenceAxis = -> Sketch036 [N_Axis]
  Refine = true
  Suppressed = false
  Type = 0
FEATURE [PartDesign::Fillet] Fillet005
  Base = -> Pad019 [Edge27,Edge25,Edge28,Edge26]
  BaseFeature = -> Pad019
  Radius = 1.8
  Refine = true
  SupportTransform = false
  Suppressed = false
  UseAllEdges = false
FEATURE [Sketcher::SketchObject] Sketch037
  ArcFitTolerance = 1e-06
  AttachmentSupport = -> [Fillet005]
  ExternalGeometry = -> [Fillet005]
  FullyConstrained = true
  MakeInternals = false
  MapMode = 5
  Placement = pos=(0,0,5) rot=(0,0,1;0rad)
  sketch-geometry (5):
    g0: Circle CenterX=-14.34 CenterY=23.5354 CenterZ=0 NormalX=0 NormalY=0 NormalZ=1 AngleXU=0 Radius=1.1
    g1: Circle CenterX=-14.34 CenterY=0.64 CenterZ=0 NormalX=0 NormalY=0 NormalZ=1 AngleXU=0 Radius=1.1
    g2: Circle CenterX=43.7012 CenterY=0.64 CenterZ=0 NormalX=0 NormalY=0 NormalZ=1 AngleXU=0 Radius=1.1
    g3: Circle CenterX=43.7012 CenterY=23.5354 CenterZ=0 NormalX=0 NormalY=0 NormalZ=1 AngleXU=0 Radius=2.5
    g4: Circle CenterX=43.7012 CenterY=23.5354 CenterZ=0 NormalX=0 NormalY=0 NormalZ=1 AngleXU=0 Radius=1.1
  constraints (10):
    c: Coincident(g0,g-3)
    c: Coincident(g1,g-4)
    c: Coincident(g2,g-5)
    c: Coincident(g3,g-6)
    c: Equal(g3,g-6)
    c: Coincident(g4,g3)
    c: Equal(g4,g2)
    c: Equal(g2,g1)
    c: Equal(g1,g0)
    c: Diameter(g0) = 2.2
FEATURE [Sketcher::SketchObject] Sketch038
  ArcFitTolerance = 1e-06
  AttachmentSupport = -> [Fillet005]
  FullyConstrained = false
  MakeInternals = false
  MapMode = 5
  Placement = pos=(49,0,0) rot=(0.57735,0.57735,0.57735;2.0944rad)
  sketch-geometry (10):
    g0: LineSegment StartX=2.91329 StartY=6.47769 StartZ=0 EndX=2.91329 EndY=6.02564 EndZ=0
    g1: LineSegment StartX=4.33325 StartY=4.60568 StartZ=0 EndX=16.0538 EndY=4.60568 EndZ=0
    g2: LineSegment StartX=17.4737 StartY=6.02564 StartZ=0 EndX=17.4737 EndY=6.47769 EndZ=0
    g3: LineSegment StartX=16.0538 StartY=7.89764 StartZ=0 EndX=4.33325 EndY=7.89764 EndZ=0
    g4: ArcOfCircle CenterX=4.33325 CenterY=6.47769 CenterZ=0 NormalX=0 NormalY=0 NormalZ=1 AngleXU=0 Radius=1.41996 StartAngle=1.5708 EndAngle=3.14159
    g5: ArcOfCircle CenterX=4.33325 CenterY=6.02564 CenterZ=0 NormalX=0 NormalY=0 NormalZ=1 AngleXU=0 Radius=1.41996 StartAngle=3.14159 EndAngle=4.71239
    g6: ArcOfCircle CenterX=16.0538 CenterY=6.02564 CenterZ=0 NormalX=0 NormalY=0 NormalZ=1 AngleXU=0 Radius=1.41996 StartAngle=4.71239 EndAngle=6.28319
    g7: ArcOfCircle CenterX=16.0538 CenterY=6.47769 CenterZ=0 NormalX=0 NormalY=0 NormalZ=1 AngleXU=0 Radius=1.41996 StartAngle=0 EndAngle=1.5708
    g8: GeomPoint [constr] X=2.91329 Y=7.89764 Z=0
    g9: GeomPoint [constr] X=17.4737 Y=4.60568 Z=0
  constraints (19):
    c: Tangent(g0,g4) = -1.5708
    c: Tangent(g0,g5) = -1.5708
    c: Tangent(g1,g5) = -1.5708
    c: Tangent(g1,g6) = -1.5708
    c: Tangent(g2,g6) = -1.5708
    c: Tangent(g2,g7) = -1.5708
    c: Tangent(g3,g7) = -1.5708
    c: Tangent(g3,g4) = -1.5708
    c: Vertical(g0)
    c: Vertical(g2)
    c: Horizontal(g1)
    c: Horizontal(g3)
    c: Equal(g4,g5)
    c: Equal(g5,g6)
    c: Equal(g6,g7)
    c: PointOnObject(g8,g0)
    c: PointOnObject(g8,g3)
    c: PointOnObject(g9,g1)
    c: PointOnObject(g9,g2)
FEATURE [PartDesign::Pocket] Pocket012
  BaseFeature = -> Fillet005
  Direction = (-1,0,0)
  Length = 2
  Length2 = 5
  Profile = -> Sketch038
  ReferenceAxis = -> Sketch038 [N_Axis]
  Refine = true
  Suppressed = false
  Type = 0
FEATURE [Sketcher::SketchObject] Sketch039
  ArcFitTolerance = 1e-06
  AttachmentSupport = -> [Pocket012]
  FullyConstrained = false
  MakeInternals = false
  MapMode = 5
  Placement = pos=(0,29.5,0) rot=(0,0.707107,0.707107;3.14159rad)
  sketch-geometry (30):
    g0: LineSegment StartX=-41.6346 StartY=7.90836 StartZ=0 EndX=-41.6346 EndY=6.62874 EndZ=0
    g1: LineSegment StartX=-39.9196 StartY=4.9138 StartZ=0 EndX=-29.6703 EndY=4.9138 EndZ=0
    g2: LineSegment StartX=-27.9554 StartY=6.62874 StartZ=0 EndX=-27.9554 EndY=7.90836 EndZ=0
    g3: LineSegment StartX=-29.6703 StartY=9.62329 StartZ=0 EndX=-39.9196 EndY=9.62329 EndZ=0
    g4: ArcOfCircle CenterX=-39.9196 CenterY=7.90836 CenterZ=0 NormalX=0 NormalY=0 NormalZ=1 AngleXU=0 Radius=1.71494 StartAngle=1.5708 EndAngle=3.14159
    g5: ArcOfCircle CenterX=-39.9196 CenterY=6.62874 CenterZ=0 NormalX=0 NormalY=0 NormalZ=1 AngleXU=0 Radius=1.71494 StartAngle=3.14159 EndAngle=4.71239
    g6: ArcOfCircle CenterX=-29.6703 CenterY=6.62874 CenterZ=0 NormalX=0 NormalY=0 NormalZ=1 AngleXU=0 Radius=1.71494 StartAngle=4.71239 EndAngle=6.28319
    g7: ArcOfCircle CenterX=-29.6703 CenterY=7.90836 CenterZ=0 NormalX=0 NormalY=0 NormalZ=1 AngleXU=0 Radius=1.71494 StartAngle=2e-16 EndAngle=1.5708
    g8: GeomPoint [constr] X=-41.6346 Y=9.62329 Z=0
    g9: GeomPoint [constr] X=-27.9554 Y=4.9138 Z=0
    g10: LineSegment StartX=-10.0767 StartY=6.97224 StartZ=0 EndX=-10.0767 EndY=6.13545 EndZ=0
    g11: LineSegment StartX=-8.85509 StartY=4.9138 StartZ=0 EndX=-2.72372 EndY=4.9138 EndZ=0
    g12: LineSegment StartX=-1.50207 StartY=6.13545 StartZ=0 EndX=-1.50207 EndY=6.97224 EndZ=0
    g13: LineSegment StartX=-2.72372 StartY=8.19389 StartZ=0 EndX=-8.85509 EndY=8.19389 EndZ=0
    g14: ArcOfCircle CenterX=-8.85509 CenterY=6.97224 CenterZ=0 NormalX=0 NormalY=0 NormalZ=1 AngleXU=0 Radius=1.22165 StartAngle=1.5708 EndAngle=3.14159
    g15: ArcOfCircle CenterX=-8.85509 CenterY=6.13545 CenterZ=0 NormalX=0 NormalY=0 NormalZ=1 AngleXU=0 Radius=1.22165 StartAngle=3.14159 EndAngle=4.71239
    g16: ArcOfCircle CenterX=-2.72372 CenterY=6.13545 CenterZ=0 NormalX=0 NormalY=0 NormalZ=1 AngleXU=0 Radius=1.22165 StartAngle=4.71239 EndAngle=6.28319
    g17: ArcOfCircle CenterX=-2.72372 CenterY=6.97224 CenterZ=0 NormalX=0 NormalY=0 NormalZ=1 AngleXU=0 Radius=1.22165 StartAngle=0 EndAngle=1.5708
    g18: GeomPoint [constr] X=-10.0767 Y=8.19389 Z=0
    g19: GeomPoint [constr] X=-1.50207 Y=4.9138 Z=0
    g20: LineSegment StartX=2.47401 StartY=6.96844 StartZ=0 EndX=2.47401 EndY=6.13925 EndZ=0
    g21: LineSegment StartX=3.69946 StartY=4.9138 StartZ=0 EndX=9.82937 EndY=4.9138 EndZ=0
    g22: LineSegment StartX=11.0548 StartY=6.13925 StartZ=0 EndX=11.0548 EndY=6.96844 EndZ=0
    g23: LineSegment StartX=9.82937 StartY=8.19389 StartZ=0 EndX=3.69946 EndY=8.19389 EndZ=0
    g24: ArcOfCircle CenterX=3.69946 CenterY=6.96844 CenterZ=0 NormalX=0 NormalY=0 NormalZ=1 AngleXU=0 Radius=1.22545 StartAngle=1.5708 EndAngle=3.14159
    g25: ArcOfCircle CenterX=3.69946 CenterY=6.13925 CenterZ=0 NormalX=0 NormalY=0 NormalZ=1 AngleXU=0 Radius=1.22545 StartAngle=3.14159 EndAngle=4.71239
    g26: ArcOfCircle CenterX=9.82937 CenterY=6.13925 CenterZ=0 NormalX=0 NormalY=0 NormalZ=1 AngleXU=0 Radius=1.22545 StartAngle=4.71239 EndAngle=6.28319
    g27: ArcOfCircle CenterX=9.82937 CenterY=6.96844 CenterZ=0 NormalX=0 NormalY=0 NormalZ=1 AngleXU=0 Radius=1.22545 StartAngle=0 EndAngle=1.5708
    g28: GeomPoint [constr] X=2.47401 Y=8.19389 Z=0
    g29: GeomPoint [constr] X=11.0548 Y=4.9138 Z=0
  constraints (60):
    c: Tangent(g0,g4) = -1.5708
    c: Tangent(g0,g5) = -1.5708
    c: Tangent(g1,g5) = -1.5708
    c: Tangent(g1,g6) = -1.5708
    c: Tangent(g2,g6) = -1.5708
    c: Tangent(g2,g7) = -1.5708
    c: Tangent(g3,g7) = -1.5708
    c: Tangent(g3,g4) = -1.5708
    c: Vertical(g0)
    c: Vertical(g2)
    c: Horizontal(g1)
    c: Horizontal(g3)
    c: Equal(g4,g5)
    c: Equal(g5,g6)
    c: Equal(g6,g7)
    c: PointOnObject(g8,g0)
    c: PointOnObject(g8,g3)
    c: PointOnObject(g9,g1)
    c: PointOnObject(g9,g2)
    c: Tangent(g10,g14) = -1.5708
    c: Tangent(g10,g15) = -1.5708
    c: Tangent(g11,g15) = -1.5708
    c: Tangent(g11,g16) = -1.5708
    c: Tangent(g12,g16) = -1.5708
    c: Tangent(g12,g17) = -1.5708
    c: Tangent(g13,g17) = -1.5708
    c: Tangent(g13,g14) = -1.5708
    c: Vertical(g10)
    c: Vertical(g12)
    c: Horizontal(g11)
    c: Horizontal(g13)
    c: Equal(g14,g15)
    c: Equal(g15,g16)
    c: Equal(g16,g17)
    c: PointOnObject(g18,g10)
    c: PointOnObject(g18,g13)
    c: PointOnObject(g19,g11)
    c: PointOnObject(g19,g12)
    c: Tangent(g20,g24) = -1.5708
    c: Tangent(g20,g25) = -1.5708
    c: Tangent(g21,g25) = -1.5708
    c: Tangent(g21,g26) = -1.5708
    c: Tangent(g22,g26) = -1.5708
    c: Tangent(g22,g27) = -1.5708
    c: Tangent(g23,g27) = -1.5708
    c: Tangent(g23,g24) = -1.5708
    c: Vertical(g20)
    c: Vertical(g22)
    c: Horizontal(g21)
    c: Horizontal(g23)
    c: Equal(g24,g25)
    c: Equal(g25,g26)
    c: Equal(g26,g27)
    c: PointOnObject(g28,g20)
    c: PointOnObject(g28,g23)
    c: PointOnObject(g29,g21)
    c: PointOnObject(g29,g22)
    c: Horizontal(g23,g13)
    c: Horizontal(g11,g21)
    c: Horizontal(g21,g1)
FEATURE [PartDesign::Pocket] Pocket013
  BaseFeature = -> Pocket012
  Direction = (0,-1,2e-16)
  Length = 2
  Length2 = 5
  Profile = -> Sketch039
  ReferenceAxis = -> Sketch039 [N_Axis]
  Refine = true
  Suppressed = false
  Type = 0
FEATURE [PartDesign::Fillet] Fillet006
  Base = -> Pocket013 [Edge104,Edge105,Edge103,Edge102,Edge101,Edge100,Edge107,Edge106,Edge111,Edge112,Edge113,Edge114,Edge108,Edge115,Edge109,Edge110,Edge121,Edge122,Edge123,Edge116,Edge120,Edge119,Edge118,Edge117,Edge80,Edge76,Edge74,Edge82,Edge84,Edge72,Edge69,Edge78]
  BaseFeature = -> Pocket013
  Radius = 1
  Refine = true
  SupportTransform = false
  Suppressed = false
  UseAllEdges = false
FEATURE [PartDesign::Body] Body007  label="Case v5"
  AllowCompound = false
  Group = -> [Sketch034,Pad018,Sketch035,Pocket011,Sketch036,Pad019,Fillet005,Sketch037,Sketch038,Pocket012,Sketch039,Pocket013,Fillet006]
  Origin = -> Origin007
  Tip = -> Fillet006
FEATURE [Measure::MeasureArea] Area  label="Area: 12.32 cm^2"
  Area = 1232
  Elements = -> [Body007]
FEATURE [Mesh::Feature] Pi_Zero_W
  Placement = pos=(49.2,28.1,4.2) rot=(0,0,1;3.14159rad)
FEATURE [Measure::MeasurePython] Center_of_Mass  label="Center_of_Mass: COM
X: -0.15 mm
Y: -0.14 mm
Z: 6.10 mm"  # WARN: FeaturePython — macro-defined, semantics opaque (R4)
  Element = -> Body007
  Placement = pos=(-0.150212,-0.137377,6.09516) rot=(0,0,1;0rad)
  Result = (-0.150212,-0.137377,6.09516)
